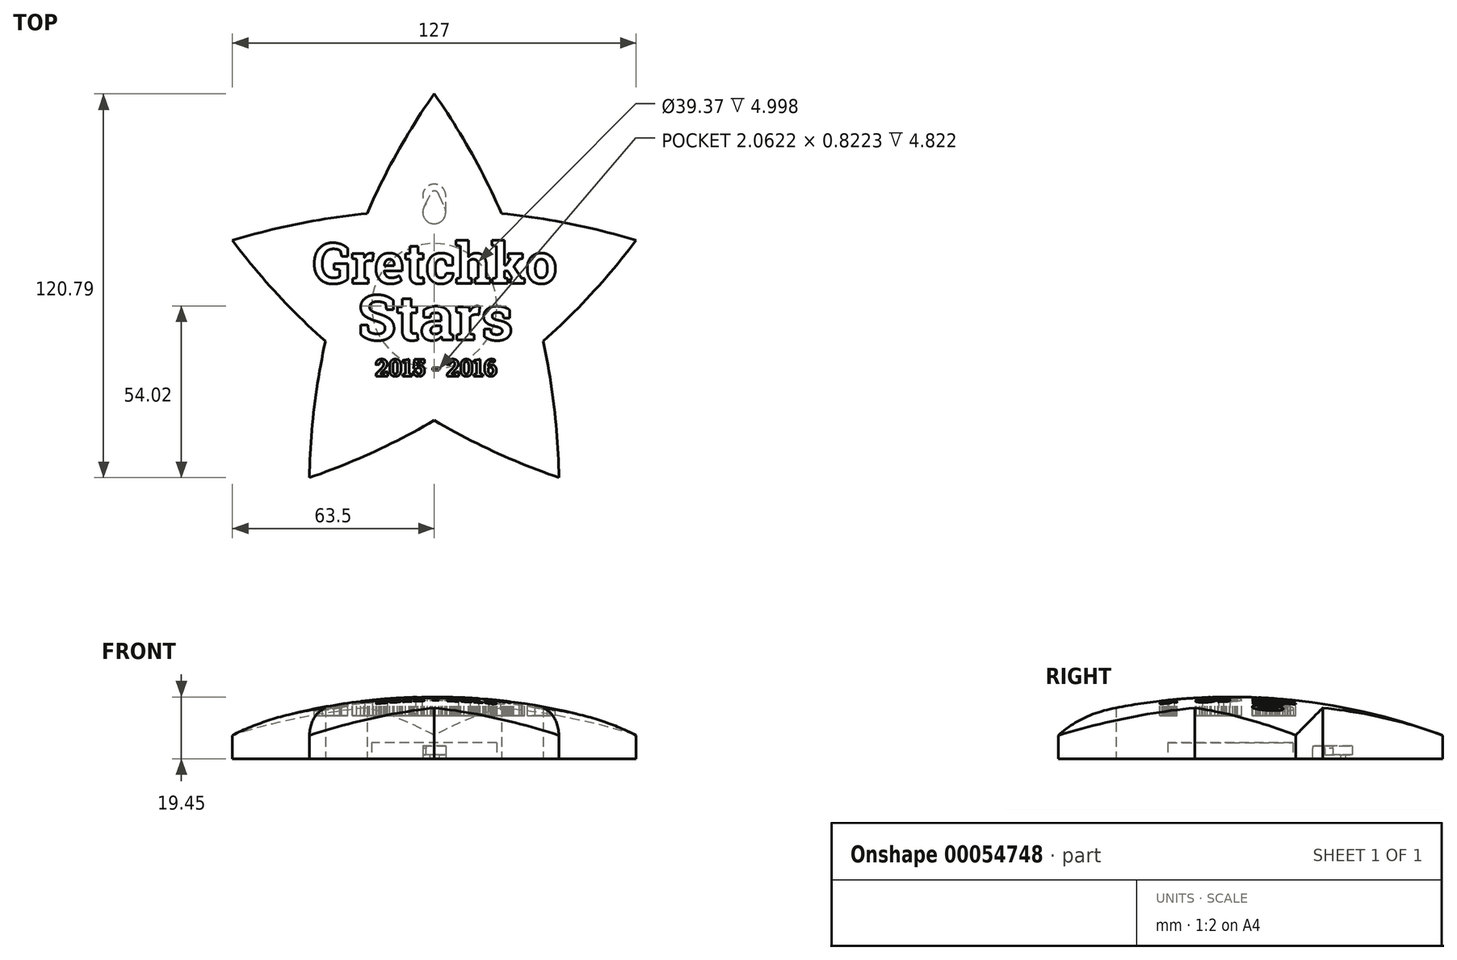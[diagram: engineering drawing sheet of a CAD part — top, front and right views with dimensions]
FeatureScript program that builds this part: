
annotation { "Feature Type Name" : "Feature", "Feature Type Description" : "" }
export const myFeature = defineFeature(function(context is Context, id is Id, definition is map)
    precondition{}
    {
        {
            var Q0;
            Q0=qCreatedBy(makeId("Top.planeOp"),FACE);
            var sketch = newSketch(context, id + "F0", { "sketchPlane" : qUnion([Q0])});
            skArc(sketch, "E0", {"start": v(39.25, -54.02) * mm, "mid": v(28.67, 9.31) * mm, "end": v(0, 66.77) * mm});
            skArc(sketch, "E1", {"start": v(0, 66.77) * mm, "mid": v(-28.67, 9.31) * mm, "end": v(-39.25, -54.02) * mm});
            skArc(sketch, "E2", {"start": v(63.5, 20.63) * mm, "mid": v(0, 30.14) * mm, "end": v(-63.5, 20.63) * mm});
            skArc(sketch, "E3", {"start": v(-63.5, 20.63) * mm, "mid": v(-17.72, -24.39) * mm, "end": v(39.25, -54.02) * mm});
            skArc(sketch, "E4", {"start": v(-39.25, -54.02) * mm, "mid": v(17.72, -24.39) * mm, "end": v(63.5, 20.63) * mm});
            skSolve(sketch);
        }
        {
            var Q0;
            Q0 = qSketchRegion(id + "F0", true);
            extrude(context, id + "F1", {"entities" : qUnion([Q0]), "depth" : 67.5 * mm});
        }
        {
            var Q0;
            Q0=qCreatedBy(makeId("Top.planeOp"),FACE);
            var sketch = newSketch(context, id + "F2", { "sketchPlane" : qUnion([Q0])});
            skCircle(sketch, "E5", {"center": v(0, 0) * mm, "radius": 190.5 * mm});
            skLineSegment(sketch, "E6", {"start": v(0, 190.5) * mm, "end": v(0, -190.5) * mm});
            skSolve(sketch);
        }
        {
            var Q0;
            Q0=makeQuery(id+"F1.opExtrude","SWEPT_BODY",BODY,{"disambiguationData":[OSD([sQuery(id+"F0.wireOp",EDGE,"E0"),sQuery(id+"F0.wireOp",EDGE,"E1"),sQuery(id+"F0.wireOp",EDGE,"E2"),sQuery(id+"F0.wireOp",EDGE,"E3"),sQuery(id+"F0.wireOp",EDGE,"E4")])]});
            var Q1;
            Q1=makeQuery(id+"F1.opExtrude","SWEPT_EDGE",EDGE,{"disambiguationData":[OSD([sQuery(id+"F0.wireOp",EDGE,"E2"),sQuery(id+"F0.wireOp",EDGE,"E3")])]});
            var Q2;
            Q2=makeQuery(id+"F1.opExtrude","CAP_FACE",FACE,{"disambiguationData":[OSD([sQuery(id+"F0.wireOp",EDGE,"E0"),sQuery(id+"F0.wireOp",EDGE,"E1"),sQuery(id+"F0.wireOp",EDGE,"E2"),sQuery(id+"F0.wireOp",EDGE,"E3"),sQuery(id+"F0.wireOp",EDGE,"E4")])],"isStart":false});
            transform(context, id + "F3", {"entities" : qUnion([Q0]), "transformType" : TransformType.TRANSLATION_DISTANCE, "transformDirection" : qUnion([Q2]), "distance" : 171.05 * mm, "makeCopy" : false});
        }
        {
            var Q0;
            {var subQ0=sQuery(id+"F2.wireOp",EDGE,"E6");Q0=makeQuery(id+"F2.imprint","IMPRINT",FACE,{"disambiguationData":[TD([[makeQuery(id+"F2.imprint","IMPRINT",EDGE,{"derivedFrom":subQ0}),-1.0]])]});}
            var Q1;
            Q1=sQuery(id+"F2.wireOp",EDGE,"E6");
            revolve(context, id + "F4", {"entities" : qUnion([Q0]), "axis" : qUnion([Q1]), "revolveType" : RevolveType.FULL});
        }
        {
            var Q0;
            Q0=makeQuery(id+"F1.opExtrude","SWEPT_BODY",BODY,{"disambiguationData":[OSD([sQuery(id+"F0.wireOp",EDGE,"E0"),sQuery(id+"F0.wireOp",EDGE,"E1"),sQuery(id+"F0.wireOp",EDGE,"E2"),sQuery(id+"F0.wireOp",EDGE,"E3"),sQuery(id+"F0.wireOp",EDGE,"E4")])]});
            var Q1;
            Q1=makeQuery(id+"F4.opRevolve","SWEPT_BODY",BODY,{"disambiguationData":[OSD([sQuery(id+"F2.wireOp",EDGE,"E5"),sQuery(id+"F2.wireOp",EDGE,"E6")])]});
            booleanBodies(context, id + "F5", {"operationType" : BooleanOperationType.INTERSECTION, "tools" : qUnion([Q0, Q1])});
        }
        {
            var Q0;
            Q0=qCreatedBy(makeId("Top.planeOp"),FACE);
            var sketch = newSketch(context, id + "F6", { "sketchPlane" : qUnion([Q0])});
            skText(sketch, "E7", { "text": "Gretchko", "fontName": "RobotoSlab-Bold.ttf"});
            skLineSegment(sketch, "E8", {"start": v(0, 0) * mm, "end": v(0, 66.71) * mm});
            const initialGuessF6  = {"E7": [-0.03813, 0.0071, 1, 0, 0.0128]};
            skSetInitialGuess(sketch, initialGuessF6);
            skSolve(sketch);
        }
        {
            var Q0;
            Q0=qCreatedBy(makeId("Top.planeOp"),FACE);
            var sketch = newSketch(context, id + "F7", { "sketchPlane" : qUnion([Q0])});
            skText(sketch, "E9", { "text": "Stars", "fontName": "RobotoSlab-Bold.ttf"});
            const initialGuessF7  = {"E9": [-0.02408, -0.01073, 1, 0, 0.01428]};
            skSetInitialGuess(sketch, initialGuessF7);
            skSolve(sketch);
        }
        {
            var Q0;
            Q0=qCreatedBy(makeId("Top.planeOp"),FACE);
            var sketch = newSketch(context, id + "F8", { "sketchPlane" : qUnion([Q0])});
            skText(sketch, "E10", { "text": "2015 - 2016", "fontName": "RobotoSlab-Bold.ttf"});
            const initialGuessF8  = {"E10": [-0.01854, -0.0221, 1, 0, 0.00539]};
            skSetInitialGuess(sketch, initialGuessF8);
            skSolve(sketch);
        }
        {
            var Q0;
            Q0=makeQuery(id+"F5.opBoolean","INTERSECT",BODY,{"derivedFrom":[makeQuery(id+"F1.opExtrude","SWEPT_BODY",BODY,{"disambiguationData":[OSD([sQuery(id+"F0.wireOp",EDGE,"E0"),sQuery(id+"F0.wireOp",EDGE,"E1"),sQuery(id+"F0.wireOp",EDGE,"E2"),sQuery(id+"F0.wireOp",EDGE,"E3"),sQuery(id+"F0.wireOp",EDGE,"E4")])]}),makeQuery(id+"F4.opRevolve","SWEPT_BODY",BODY,{"disambiguationData":[OSD([sQuery(id+"F2.wireOp",EDGE,"E5"),sQuery(id+"F2.wireOp",EDGE,"E6")])]})]});
            var Q1;
            Q1=qCreatedBy(makeId("Top.planeOp"),FACE);
            transform(context, id + "F9", {"entities" : qUnion([Q0]), "transformType" : TransformType.TRANSLATION_DISTANCE, "transformDirection" : qUnion([Q1]), "distance" : 221.94 * mm, "oppositeDirection" : true, "makeCopy" : false});
        }
        {
            var Q0;
            Q0=makeQuery(id+"F6.imprint","IMPRINT",FACE,{"disambiguationData":[TD([[makeQuery(id+"F6.imprint","IMPRINT",EDGE,{"derivedFrom":sQuery(id+"F6.wireOp",EDGE,"E7.sketch_text.stroke-0")}),-1.0]])]});
            var Q1;
            Q1=makeQuery(id+"F6.imprint","IMPRINT",FACE,{"disambiguationData":[TD([[makeQuery(id+"F6.imprint","IMPRINT",EDGE,{"derivedFrom":sQuery(id+"F6.wireOp",EDGE,"E7.sketch_text.stroke-26")}),-1.0]])]});
            var Q2;
            Q2=makeQuery(id+"F6.imprint","IMPRINT",FACE,{"disambiguationData":[TD([[makeQuery(id+"F6.imprint","IMPRINT",EDGE,{"derivedFrom":sQuery(id+"F6.wireOp",EDGE,"E7.sketch_text.stroke-69")}),-1.0]])]});
            var Q3;
            Q3=makeQuery(id+"F6.imprint","IMPRINT",FACE,{"disambiguationData":[TD([[makeQuery(id+"F6.imprint","IMPRINT",EDGE,{"derivedFrom":sQuery(id+"F6.wireOp",EDGE,"E7.sketch_text.stroke-112")}),-1.0]])]});
            var Q4;
            Q4=makeQuery(id+"F6.imprint","IMPRINT",FACE,{"disambiguationData":[TD([[makeQuery(id+"F6.imprint","IMPRINT",EDGE,{"derivedFrom":sQuery(id+"F6.wireOp",EDGE,"E7.sketch_text.stroke-138")}),-1.0]])]});
            var Q5;
            Q5=makeQuery(id+"F6.imprint","IMPRINT",FACE,{"disambiguationData":[TD([[makeQuery(id+"F6.imprint","IMPRINT",EDGE,{"derivedFrom":sQuery(id+"F6.wireOp",EDGE,"E7.sketch_text.stroke-45")}),-1.0]])]});
            var Q6;
            Q6=makeQuery(id+"F6.imprint","IMPRINT",FACE,{"disambiguationData":[TD([[makeQuery(id+"F6.imprint","IMPRINT",EDGE,{"derivedFrom":sQuery(id+"F6.wireOp",EDGE,"E7.sketch_text.stroke-89")}),-1.0]])]});
            var Q7;
            {var subQ1=sQuery(id+"F6.wireOp",EDGE,"E7.sketch_text.stroke-96");Q7=makeQuery(id+"F6.imprint","IMPRINT",FACE,{"disambiguationData":[TD([[makeQuery(id+"F6.imprint","IMPRINT",EDGE,{"derivedFrom":subQ1}),-1.0]])]});}
            var Q8;
            Q8=makeQuery(id+"F6.imprint","IMPRINT",FACE,{"disambiguationData":[TD([[makeQuery(id+"F6.imprint","IMPRINT",EDGE,{"derivedFrom":sQuery(id+"F6.wireOp",EDGE,"E7.sketch_text.stroke-165")}),-1.0]])]});
            var Q9;
            Q9=makeQuery(id+"F7.imprint","IMPRINT",FACE,{"disambiguationData":[TD([[makeQuery(id+"F7.imprint","IMPRINT",EDGE,{"derivedFrom":sQuery(id+"F7.wireOp",EDGE,"E9.sketch_text.stroke-0")}),-1.0]])]});
            var Q10;
            Q10=makeQuery(id+"F7.imprint","IMPRINT",FACE,{"disambiguationData":[TD([[makeQuery(id+"F7.imprint","IMPRINT",EDGE,{"derivedFrom":sQuery(id+"F7.wireOp",EDGE,"E9.sketch_text.stroke-30")}),-1.0]])]});
            var Q11;
            Q11=makeQuery(id+"F7.imprint","IMPRINT",FACE,{"disambiguationData":[TD([[makeQuery(id+"F7.imprint","IMPRINT",EDGE,{"derivedFrom":sQuery(id+"F7.wireOp",EDGE,"E9.sketch_text.stroke-85")}),-1.0]])]});
            var Q12;
            Q12=makeQuery(id+"F7.imprint","IMPRINT",FACE,{"disambiguationData":[TD([[makeQuery(id+"F7.imprint","IMPRINT",EDGE,{"derivedFrom":sQuery(id+"F7.wireOp",EDGE,"E9.sketch_text.stroke-104")}),-1.0]])]});
            var Q13;
            Q13=makeQuery(id+"F7.imprint","IMPRINT",FACE,{"disambiguationData":[TD([[makeQuery(id+"F7.imprint","IMPRINT",EDGE,{"derivedFrom":sQuery(id+"F7.wireOp",EDGE,"E9.sketch_text.stroke-50")}),-1.0]])]});
            var Q14;
            Q14=makeQuery(id+"F8.imprint","IMPRINT",FACE,{"disambiguationData":[TD([[makeQuery(id+"F8.imprint","IMPRINT",EDGE,{"derivedFrom":sQuery(id+"F8.wireOp",EDGE,"E10.sketch_text.stroke-0")}),-1.0]])]});
            var Q15;
            Q15=makeQuery(id+"F8.imprint","IMPRINT",FACE,{"disambiguationData":[TD([[makeQuery(id+"F8.imprint","IMPRINT",EDGE,{"derivedFrom":sQuery(id+"F8.wireOp",EDGE,"E10.sketch_text.stroke-43")}),-1.0]])]});
            var Q16;
            Q16=makeQuery(id+"F8.imprint","IMPRINT",FACE,{"disambiguationData":[TD([[makeQuery(id+"F8.imprint","IMPRINT",EDGE,{"derivedFrom":sQuery(id+"F8.wireOp",EDGE,"E10.sketch_text.stroke-53")}),-1.0]])]});
            var Q17;
            Q17=makeQuery(id+"F8.imprint","IMPRINT",FACE,{"disambiguationData":[TD([[makeQuery(id+"F8.imprint","IMPRINT",EDGE,{"derivedFrom":sQuery(id+"F8.wireOp",EDGE,"E10.sketch_text.stroke-79")}),-1.0]])]});
            var Q18;
            Q18=makeQuery(id+"F8.imprint","IMPRINT",FACE,{"disambiguationData":[TD([[makeQuery(id+"F8.imprint","IMPRINT",EDGE,{"derivedFrom":sQuery(id+"F8.wireOp",EDGE,"E10.sketch_text.stroke-83")}),-1.0]])]});
            var Q19;
            Q19=makeQuery(id+"F8.imprint","IMPRINT",FACE,{"disambiguationData":[TD([[makeQuery(id+"F8.imprint","IMPRINT",EDGE,{"derivedFrom":sQuery(id+"F8.wireOp",EDGE,"E10.sketch_text.stroke-126")}),-1.0]])]});
            var Q20;
            Q20=makeQuery(id+"F8.imprint","IMPRINT",FACE,{"disambiguationData":[TD([[makeQuery(id+"F8.imprint","IMPRINT",EDGE,{"derivedFrom":sQuery(id+"F8.wireOp",EDGE,"E10.sketch_text.stroke-23")}),-1.0]])]});
            var Q21;
            Q21=makeQuery(id+"F8.imprint","IMPRINT",FACE,{"disambiguationData":[TD([[makeQuery(id+"F8.imprint","IMPRINT",EDGE,{"derivedFrom":sQuery(id+"F8.wireOp",EDGE,"E10.sketch_text.stroke-106")}),-1.0]])]});
            var Q22;
            Q22=makeQuery(id+"F8.imprint","IMPRINT",FACE,{"disambiguationData":[TD([[makeQuery(id+"F8.imprint","IMPRINT",EDGE,{"derivedFrom":sQuery(id+"F8.wireOp",EDGE,"E10.sketch_text.stroke-136")}),-1.0]])]});
            extrude(context, id + "F10", {"entities" : qUnion([Q0, Q1, Q2, Q3, Q4, Q5, Q6, Q7, Q8, Q9, Q10, Q11, Q12, Q13, Q14, Q15, Q16, Q17, Q18, Q19, Q20, Q21, Q22]), "operationType" : NewBodyOperationType.ADD, "oppositeDirection" : true, "depth" : 15.68 * mm});
        }
        {
            var Q0;
            Q0=makeQuery(id+"F10.opExtrude","SWEPT_BODY",BODY,{"disambiguationData":[OSD([sQuery(id+"F6.wireOp",EDGE,"E7.sketch_text.stroke-0"),sQuery(id+"F6.wireOp",EDGE,"E7.sketch_text.stroke-1"),sQuery(id+"F6.wireOp",EDGE,"E7.sketch_text.stroke-2"),sQuery(id+"F6.wireOp",EDGE,"E7.sketch_text.stroke-3"),sQuery(id+"F6.wireOp",EDGE,"E7.sketch_text.stroke-4"),sQuery(id+"F6.wireOp",EDGE,"E7.sketch_text.stroke-5"),sQuery(id+"F6.wireOp",EDGE,"E7.sketch_text.stroke-6"),sQuery(id+"F6.wireOp",EDGE,"E7.sketch_text.stroke-7"),sQuery(id+"F6.wireOp",EDGE,"E7.sketch_text.stroke-8"),sQuery(id+"F6.wireOp",EDGE,"E7.sketch_text.stroke-9"),sQuery(id+"F6.wireOp",EDGE,"E7.sketch_text.stroke-10"),sQuery(id+"F6.wireOp",EDGE,"E7.sketch_text.stroke-11"),sQuery(id+"F6.wireOp",EDGE,"E7.sketch_text.stroke-12"),sQuery(id+"F6.wireOp",EDGE,"E7.sketch_text.stroke-13"),sQuery(id+"F6.wireOp",EDGE,"E7.sketch_text.stroke-14"),sQuery(id+"F6.wireOp",EDGE,"E7.sketch_text.stroke-15"),sQuery(id+"F6.wireOp",EDGE,"E7.sketch_text.stroke-16"),sQuery(id+"F6.wireOp",EDGE,"E7.sketch_text.stroke-17"),sQuery(id+"F6.wireOp",EDGE,"E7.sketch_text.stroke-18"),sQuery(id+"F6.wireOp",EDGE,"E7.sketch_text.stroke-19"),sQuery(id+"F6.wireOp",EDGE,"E7.sketch_text.stroke-20"),sQuery(id+"F6.wireOp",EDGE,"E7.sketch_text.stroke-21"),sQuery(id+"F6.wireOp",EDGE,"E7.sketch_text.stroke-22"),sQuery(id+"F6.wireOp",EDGE,"E7.sketch_text.stroke-23"),sQuery(id+"F6.wireOp",EDGE,"E7.sketch_text.stroke-24"),sQuery(id+"F6.wireOp",EDGE,"E7.sketch_text.stroke-25")])]});
            var Q1;
            Q1=makeQuery(id+"F10.opExtrude","SWEPT_BODY",BODY,{"disambiguationData":[OSD([sQuery(id+"F6.wireOp",EDGE,"E7.sketch_text.stroke-26"),sQuery(id+"F6.wireOp",EDGE,"E7.sketch_text.stroke-27"),sQuery(id+"F6.wireOp",EDGE,"E7.sketch_text.stroke-28"),sQuery(id+"F6.wireOp",EDGE,"E7.sketch_text.stroke-29"),sQuery(id+"F6.wireOp",EDGE,"E7.sketch_text.stroke-30"),sQuery(id+"F6.wireOp",EDGE,"E7.sketch_text.stroke-31"),sQuery(id+"F6.wireOp",EDGE,"E7.sketch_text.stroke-32"),sQuery(id+"F6.wireOp",EDGE,"E7.sketch_text.stroke-33"),sQuery(id+"F6.wireOp",EDGE,"E7.sketch_text.stroke-34"),sQuery(id+"F6.wireOp",EDGE,"E7.sketch_text.stroke-35"),sQuery(id+"F6.wireOp",EDGE,"E7.sketch_text.stroke-36"),sQuery(id+"F6.wireOp",EDGE,"E7.sketch_text.stroke-37"),sQuery(id+"F6.wireOp",EDGE,"E7.sketch_text.stroke-38"),sQuery(id+"F6.wireOp",EDGE,"E7.sketch_text.stroke-39"),sQuery(id+"F6.wireOp",EDGE,"E7.sketch_text.stroke-40"),sQuery(id+"F6.wireOp",EDGE,"E7.sketch_text.stroke-41"),sQuery(id+"F6.wireOp",EDGE,"E7.sketch_text.stroke-42"),sQuery(id+"F6.wireOp",EDGE,"E7.sketch_text.stroke-43"),sQuery(id+"F6.wireOp",EDGE,"E7.sketch_text.stroke-44")])]});
            var Q2;
            Q2=makeQuery(id+"F10.opExtrude","SWEPT_BODY",BODY,{"disambiguationData":[OSD([sQuery(id+"F6.wireOp",EDGE,"E7.sketch_text.stroke-45"),sQuery(id+"F6.wireOp",EDGE,"E7.sketch_text.stroke-46"),sQuery(id+"F6.wireOp",EDGE,"E7.sketch_text.stroke-47"),sQuery(id+"F6.wireOp",EDGE,"E7.sketch_text.stroke-48"),sQuery(id+"F6.wireOp",EDGE,"E7.sketch_text.stroke-49"),sQuery(id+"F6.wireOp",EDGE,"E7.sketch_text.stroke-50"),sQuery(id+"F6.wireOp",EDGE,"E7.sketch_text.stroke-51"),sQuery(id+"F6.wireOp",EDGE,"E7.sketch_text.stroke-52"),sQuery(id+"F6.wireOp",EDGE,"E7.sketch_text.stroke-53"),sQuery(id+"F6.wireOp",EDGE,"E7.sketch_text.stroke-54"),sQuery(id+"F6.wireOp",EDGE,"E7.sketch_text.stroke-55"),sQuery(id+"F6.wireOp",EDGE,"E7.sketch_text.stroke-56"),sQuery(id+"F6.wireOp",EDGE,"E7.sketch_text.stroke-57"),sQuery(id+"F6.wireOp",EDGE,"E7.sketch_text.stroke-58"),sQuery(id+"F6.wireOp",EDGE,"E7.sketch_text.stroke-59"),sQuery(id+"F6.wireOp",EDGE,"E7.sketch_text.stroke-60"),sQuery(id+"F6.wireOp",EDGE,"E7.sketch_text.stroke-61"),sQuery(id+"F6.wireOp",EDGE,"E7.sketch_text.stroke-62"),sQuery(id+"F6.wireOp",EDGE,"E7.sketch_text.stroke-63"),sQuery(id+"F6.wireOp",EDGE,"E7.sketch_text.stroke-64"),sQuery(id+"F6.wireOp",EDGE,"E7.sketch_text.stroke-65"),sQuery(id+"F6.wireOp",EDGE,"E7.sketch_text.stroke-66"),sQuery(id+"F6.wireOp",EDGE,"E7.sketch_text.stroke-67"),sQuery(id+"F6.wireOp",EDGE,"E7.sketch_text.stroke-68")])]});
            var Q3;
            Q3=makeQuery(id+"F10.opExtrude","SWEPT_BODY",BODY,{"disambiguationData":[OSD([sQuery(id+"F6.wireOp",EDGE,"E7.sketch_text.stroke-69"),sQuery(id+"F6.wireOp",EDGE,"E7.sketch_text.stroke-70"),sQuery(id+"F6.wireOp",EDGE,"E7.sketch_text.stroke-71"),sQuery(id+"F6.wireOp",EDGE,"E7.sketch_text.stroke-72"),sQuery(id+"F6.wireOp",EDGE,"E7.sketch_text.stroke-73"),sQuery(id+"F6.wireOp",EDGE,"E7.sketch_text.stroke-74"),sQuery(id+"F6.wireOp",EDGE,"E7.sketch_text.stroke-75"),sQuery(id+"F6.wireOp",EDGE,"E7.sketch_text.stroke-76"),sQuery(id+"F6.wireOp",EDGE,"E7.sketch_text.stroke-77"),sQuery(id+"F6.wireOp",EDGE,"E7.sketch_text.stroke-78"),sQuery(id+"F6.wireOp",EDGE,"E7.sketch_text.stroke-79"),sQuery(id+"F6.wireOp",EDGE,"E7.sketch_text.stroke-80"),sQuery(id+"F6.wireOp",EDGE,"E7.sketch_text.stroke-81"),sQuery(id+"F6.wireOp",EDGE,"E7.sketch_text.stroke-82"),sQuery(id+"F6.wireOp",EDGE,"E7.sketch_text.stroke-83"),sQuery(id+"F6.wireOp",EDGE,"E7.sketch_text.stroke-84"),sQuery(id+"F6.wireOp",EDGE,"E7.sketch_text.stroke-85"),sQuery(id+"F6.wireOp",EDGE,"E7.sketch_text.stroke-86"),sQuery(id+"F6.wireOp",EDGE,"E7.sketch_text.stroke-87"),sQuery(id+"F6.wireOp",EDGE,"E7.sketch_text.stroke-88")])]});
            var Q4;
            Q4=makeQuery(id+"F10.opExtrude","SWEPT_BODY",BODY,{"disambiguationData":[OSD([sQuery(id+"F6.wireOp",EDGE,"E7.sketch_text.stroke-89"),sQuery(id+"F6.wireOp",EDGE,"E7.sketch_text.stroke-90"),sQuery(id+"F6.wireOp",EDGE,"E7.sketch_text.stroke-91"),sQuery(id+"F6.wireOp",EDGE,"E7.sketch_text.stroke-92"),sQuery(id+"F6.wireOp",EDGE,"E7.sketch_text.stroke-93"),sQuery(id+"F6.wireOp",EDGE,"E7.sketch_text.stroke-94"),sQuery(id+"F6.wireOp",EDGE,"E7.sketch_text.stroke-95"),sQuery(id+"F6.wireOp",EDGE,"E7.sketch_text.stroke-96"),sQuery(id+"F6.wireOp",EDGE,"E7.sketch_text.stroke-97"),sQuery(id+"F6.wireOp",EDGE,"E7.sketch_text.stroke-98"),sQuery(id+"F6.wireOp",EDGE,"E7.sketch_text.stroke-99"),sQuery(id+"F6.wireOp",EDGE,"E7.sketch_text.stroke-100"),sQuery(id+"F6.wireOp",EDGE,"E7.sketch_text.stroke-101"),sQuery(id+"F6.wireOp",EDGE,"E7.sketch_text.stroke-102"),sQuery(id+"F6.wireOp",EDGE,"E7.sketch_text.stroke-103"),sQuery(id+"F6.wireOp",EDGE,"E7.sketch_text.stroke-104"),sQuery(id+"F6.wireOp",EDGE,"E7.sketch_text.stroke-105"),sQuery(id+"F6.wireOp",EDGE,"E7.sketch_text.stroke-106"),sQuery(id+"F6.wireOp",EDGE,"E7.sketch_text.stroke-107"),sQuery(id+"F6.wireOp",EDGE,"E7.sketch_text.stroke-108"),sQuery(id+"F6.wireOp",EDGE,"E7.sketch_text.stroke-109"),sQuery(id+"F6.wireOp",EDGE,"E7.sketch_text.stroke-110"),sQuery(id+"F6.wireOp",EDGE,"E7.sketch_text.stroke-111")])]});
            var Q5;
            Q5=makeQuery(id+"F10.opExtrude","SWEPT_BODY",BODY,{"disambiguationData":[OSD([sQuery(id+"F6.wireOp",EDGE,"E7.sketch_text.stroke-112"),sQuery(id+"F6.wireOp",EDGE,"E7.sketch_text.stroke-113"),sQuery(id+"F6.wireOp",EDGE,"E7.sketch_text.stroke-114"),sQuery(id+"F6.wireOp",EDGE,"E7.sketch_text.stroke-115"),sQuery(id+"F6.wireOp",EDGE,"E7.sketch_text.stroke-116"),sQuery(id+"F6.wireOp",EDGE,"E7.sketch_text.stroke-117"),sQuery(id+"F6.wireOp",EDGE,"E7.sketch_text.stroke-118"),sQuery(id+"F6.wireOp",EDGE,"E7.sketch_text.stroke-119"),sQuery(id+"F6.wireOp",EDGE,"E7.sketch_text.stroke-120"),sQuery(id+"F6.wireOp",EDGE,"E7.sketch_text.stroke-121"),sQuery(id+"F6.wireOp",EDGE,"E7.sketch_text.stroke-122"),sQuery(id+"F6.wireOp",EDGE,"E7.sketch_text.stroke-123"),sQuery(id+"F6.wireOp",EDGE,"E7.sketch_text.stroke-124"),sQuery(id+"F6.wireOp",EDGE,"E7.sketch_text.stroke-125"),sQuery(id+"F6.wireOp",EDGE,"E7.sketch_text.stroke-126"),sQuery(id+"F6.wireOp",EDGE,"E7.sketch_text.stroke-127"),sQuery(id+"F6.wireOp",EDGE,"E7.sketch_text.stroke-128"),sQuery(id+"F6.wireOp",EDGE,"E7.sketch_text.stroke-129"),sQuery(id+"F6.wireOp",EDGE,"E7.sketch_text.stroke-130"),sQuery(id+"F6.wireOp",EDGE,"E7.sketch_text.stroke-131"),sQuery(id+"F6.wireOp",EDGE,"E7.sketch_text.stroke-132"),sQuery(id+"F6.wireOp",EDGE,"E7.sketch_text.stroke-133"),sQuery(id+"F6.wireOp",EDGE,"E7.sketch_text.stroke-134"),sQuery(id+"F6.wireOp",EDGE,"E7.sketch_text.stroke-135"),sQuery(id+"F6.wireOp",EDGE,"E7.sketch_text.stroke-136"),sQuery(id+"F6.wireOp",EDGE,"E7.sketch_text.stroke-137")])]});
            var Q6;
            Q6=makeQuery(id+"F10.opExtrude","SWEPT_BODY",BODY,{"disambiguationData":[OSD([sQuery(id+"F6.wireOp",EDGE,"E7.sketch_text.stroke-138"),sQuery(id+"F6.wireOp",EDGE,"E7.sketch_text.stroke-139"),sQuery(id+"F6.wireOp",EDGE,"E7.sketch_text.stroke-140"),sQuery(id+"F6.wireOp",EDGE,"E7.sketch_text.stroke-141"),sQuery(id+"F6.wireOp",EDGE,"E7.sketch_text.stroke-142"),sQuery(id+"F6.wireOp",EDGE,"E7.sketch_text.stroke-143"),sQuery(id+"F6.wireOp",EDGE,"E7.sketch_text.stroke-144"),sQuery(id+"F6.wireOp",EDGE,"E7.sketch_text.stroke-145"),sQuery(id+"F6.wireOp",EDGE,"E7.sketch_text.stroke-146"),sQuery(id+"F6.wireOp",EDGE,"E7.sketch_text.stroke-147"),sQuery(id+"F6.wireOp",EDGE,"E7.sketch_text.stroke-148"),sQuery(id+"F6.wireOp",EDGE,"E7.sketch_text.stroke-149"),sQuery(id+"F6.wireOp",EDGE,"E7.sketch_text.stroke-150"),sQuery(id+"F6.wireOp",EDGE,"E7.sketch_text.stroke-151"),sQuery(id+"F6.wireOp",EDGE,"E7.sketch_text.stroke-152"),sQuery(id+"F6.wireOp",EDGE,"E7.sketch_text.stroke-153"),sQuery(id+"F6.wireOp",EDGE,"E7.sketch_text.stroke-154"),sQuery(id+"F6.wireOp",EDGE,"E7.sketch_text.stroke-155"),sQuery(id+"F6.wireOp",EDGE,"E7.sketch_text.stroke-156"),sQuery(id+"F6.wireOp",EDGE,"E7.sketch_text.stroke-157"),sQuery(id+"F6.wireOp",EDGE,"E7.sketch_text.stroke-158"),sQuery(id+"F6.wireOp",EDGE,"E7.sketch_text.stroke-159"),sQuery(id+"F6.wireOp",EDGE,"E7.sketch_text.stroke-160"),sQuery(id+"F6.wireOp",EDGE,"E7.sketch_text.stroke-161"),sQuery(id+"F6.wireOp",EDGE,"E7.sketch_text.stroke-162"),sQuery(id+"F6.wireOp",EDGE,"E7.sketch_text.stroke-163"),sQuery(id+"F6.wireOp",EDGE,"E7.sketch_text.stroke-164")])]});
            var Q7;
            Q7=makeQuery(id+"F10.opExtrude","SWEPT_BODY",BODY,{"disambiguationData":[OSD([sQuery(id+"F6.wireOp",EDGE,"E7.sketch_text.stroke-165"),sQuery(id+"F6.wireOp",EDGE,"E7.sketch_text.stroke-166"),sQuery(id+"F6.wireOp",EDGE,"E7.sketch_text.stroke-167"),sQuery(id+"F6.wireOp",EDGE,"E7.sketch_text.stroke-168"),sQuery(id+"F6.wireOp",EDGE,"E7.sketch_text.stroke-169"),sQuery(id+"F6.wireOp",EDGE,"E7.sketch_text.stroke-170"),sQuery(id+"F6.wireOp",EDGE,"E7.sketch_text.stroke-171"),sQuery(id+"F6.wireOp",EDGE,"E7.sketch_text.stroke-172"),sQuery(id+"F6.wireOp",EDGE,"E7.sketch_text.stroke-173"),sQuery(id+"F6.wireOp",EDGE,"E7.sketch_text.stroke-174"),sQuery(id+"F6.wireOp",EDGE,"E7.sketch_text.stroke-175"),sQuery(id+"F6.wireOp",EDGE,"E7.sketch_text.stroke-176"),sQuery(id+"F6.wireOp",EDGE,"E7.sketch_text.stroke-177"),sQuery(id+"F6.wireOp",EDGE,"E7.sketch_text.stroke-178"),sQuery(id+"F6.wireOp",EDGE,"E7.sketch_text.stroke-179"),sQuery(id+"F6.wireOp",EDGE,"E7.sketch_text.stroke-180"),sQuery(id+"F6.wireOp",EDGE,"E7.sketch_text.stroke-181"),sQuery(id+"F6.wireOp",EDGE,"E7.sketch_text.stroke-182"),sQuery(id+"F6.wireOp",EDGE,"E7.sketch_text.stroke-183"),sQuery(id+"F6.wireOp",EDGE,"E7.sketch_text.stroke-184")])]});
            var Q8;
            Q8=makeQuery(id+"F10.opExtrude","SWEPT_BODY",BODY,{"disambiguationData":[OSD([sQuery(id+"F7.wireOp",EDGE,"E9.sketch_text.stroke-0"),sQuery(id+"F7.wireOp",EDGE,"E9.sketch_text.stroke-1"),sQuery(id+"F7.wireOp",EDGE,"E9.sketch_text.stroke-2"),sQuery(id+"F7.wireOp",EDGE,"E9.sketch_text.stroke-3"),sQuery(id+"F7.wireOp",EDGE,"E9.sketch_text.stroke-4"),sQuery(id+"F7.wireOp",EDGE,"E9.sketch_text.stroke-5"),sQuery(id+"F7.wireOp",EDGE,"E9.sketch_text.stroke-6"),sQuery(id+"F7.wireOp",EDGE,"E9.sketch_text.stroke-7"),sQuery(id+"F7.wireOp",EDGE,"E9.sketch_text.stroke-8"),sQuery(id+"F7.wireOp",EDGE,"E9.sketch_text.stroke-9"),sQuery(id+"F7.wireOp",EDGE,"E9.sketch_text.stroke-10"),sQuery(id+"F7.wireOp",EDGE,"E9.sketch_text.stroke-11"),sQuery(id+"F7.wireOp",EDGE,"E9.sketch_text.stroke-12"),sQuery(id+"F7.wireOp",EDGE,"E9.sketch_text.stroke-13"),sQuery(id+"F7.wireOp",EDGE,"E9.sketch_text.stroke-14"),sQuery(id+"F7.wireOp",EDGE,"E9.sketch_text.stroke-15"),sQuery(id+"F7.wireOp",EDGE,"E9.sketch_text.stroke-16"),sQuery(id+"F7.wireOp",EDGE,"E9.sketch_text.stroke-17"),sQuery(id+"F7.wireOp",EDGE,"E9.sketch_text.stroke-18"),sQuery(id+"F7.wireOp",EDGE,"E9.sketch_text.stroke-19"),sQuery(id+"F7.wireOp",EDGE,"E9.sketch_text.stroke-20"),sQuery(id+"F7.wireOp",EDGE,"E9.sketch_text.stroke-21"),sQuery(id+"F7.wireOp",EDGE,"E9.sketch_text.stroke-22"),sQuery(id+"F7.wireOp",EDGE,"E9.sketch_text.stroke-23"),sQuery(id+"F7.wireOp",EDGE,"E9.sketch_text.stroke-24"),sQuery(id+"F7.wireOp",EDGE,"E9.sketch_text.stroke-25"),sQuery(id+"F7.wireOp",EDGE,"E9.sketch_text.stroke-26"),sQuery(id+"F7.wireOp",EDGE,"E9.sketch_text.stroke-27"),sQuery(id+"F7.wireOp",EDGE,"E9.sketch_text.stroke-28"),sQuery(id+"F7.wireOp",EDGE,"E9.sketch_text.stroke-29")])]});
            var Q9;
            Q9=makeQuery(id+"F10.opExtrude","SWEPT_BODY",BODY,{"disambiguationData":[OSD([sQuery(id+"F7.wireOp",EDGE,"E9.sketch_text.stroke-30"),sQuery(id+"F7.wireOp",EDGE,"E9.sketch_text.stroke-31"),sQuery(id+"F7.wireOp",EDGE,"E9.sketch_text.stroke-32"),sQuery(id+"F7.wireOp",EDGE,"E9.sketch_text.stroke-33"),sQuery(id+"F7.wireOp",EDGE,"E9.sketch_text.stroke-34"),sQuery(id+"F7.wireOp",EDGE,"E9.sketch_text.stroke-35"),sQuery(id+"F7.wireOp",EDGE,"E9.sketch_text.stroke-36"),sQuery(id+"F7.wireOp",EDGE,"E9.sketch_text.stroke-37"),sQuery(id+"F7.wireOp",EDGE,"E9.sketch_text.stroke-38"),sQuery(id+"F7.wireOp",EDGE,"E9.sketch_text.stroke-39"),sQuery(id+"F7.wireOp",EDGE,"E9.sketch_text.stroke-40"),sQuery(id+"F7.wireOp",EDGE,"E9.sketch_text.stroke-41"),sQuery(id+"F7.wireOp",EDGE,"E9.sketch_text.stroke-42"),sQuery(id+"F7.wireOp",EDGE,"E9.sketch_text.stroke-43"),sQuery(id+"F7.wireOp",EDGE,"E9.sketch_text.stroke-44"),sQuery(id+"F7.wireOp",EDGE,"E9.sketch_text.stroke-45"),sQuery(id+"F7.wireOp",EDGE,"E9.sketch_text.stroke-46"),sQuery(id+"F7.wireOp",EDGE,"E9.sketch_text.stroke-47"),sQuery(id+"F7.wireOp",EDGE,"E9.sketch_text.stroke-48"),sQuery(id+"F7.wireOp",EDGE,"E9.sketch_text.stroke-49")])]});
            var Q10;
            Q10=makeQuery(id+"F10.opExtrude","SWEPT_BODY",BODY,{"disambiguationData":[OSD([sQuery(id+"F7.wireOp",EDGE,"E9.sketch_text.stroke-50"),sQuery(id+"F7.wireOp",EDGE,"E9.sketch_text.stroke-51"),sQuery(id+"F7.wireOp",EDGE,"E9.sketch_text.stroke-52"),sQuery(id+"F7.wireOp",EDGE,"E9.sketch_text.stroke-53"),sQuery(id+"F7.wireOp",EDGE,"E9.sketch_text.stroke-54"),sQuery(id+"F7.wireOp",EDGE,"E9.sketch_text.stroke-55"),sQuery(id+"F7.wireOp",EDGE,"E9.sketch_text.stroke-56"),sQuery(id+"F7.wireOp",EDGE,"E9.sketch_text.stroke-57"),sQuery(id+"F7.wireOp",EDGE,"E9.sketch_text.stroke-58"),sQuery(id+"F7.wireOp",EDGE,"E9.sketch_text.stroke-59"),sQuery(id+"F7.wireOp",EDGE,"E9.sketch_text.stroke-60"),sQuery(id+"F7.wireOp",EDGE,"E9.sketch_text.stroke-61"),sQuery(id+"F7.wireOp",EDGE,"E9.sketch_text.stroke-62"),sQuery(id+"F7.wireOp",EDGE,"E9.sketch_text.stroke-63"),sQuery(id+"F7.wireOp",EDGE,"E9.sketch_text.stroke-64"),sQuery(id+"F7.wireOp",EDGE,"E9.sketch_text.stroke-65"),sQuery(id+"F7.wireOp",EDGE,"E9.sketch_text.stroke-66"),sQuery(id+"F7.wireOp",EDGE,"E9.sketch_text.stroke-67"),sQuery(id+"F7.wireOp",EDGE,"E9.sketch_text.stroke-68"),sQuery(id+"F7.wireOp",EDGE,"E9.sketch_text.stroke-69"),sQuery(id+"F7.wireOp",EDGE,"E9.sketch_text.stroke-70"),sQuery(id+"F7.wireOp",EDGE,"E9.sketch_text.stroke-71"),sQuery(id+"F7.wireOp",EDGE,"E9.sketch_text.stroke-72"),sQuery(id+"F7.wireOp",EDGE,"E9.sketch_text.stroke-73"),sQuery(id+"F7.wireOp",EDGE,"E9.sketch_text.stroke-74"),sQuery(id+"F7.wireOp",EDGE,"E9.sketch_text.stroke-75"),sQuery(id+"F7.wireOp",EDGE,"E9.sketch_text.stroke-76"),sQuery(id+"F7.wireOp",EDGE,"E9.sketch_text.stroke-77"),sQuery(id+"F7.wireOp",EDGE,"E9.sketch_text.stroke-78"),sQuery(id+"F7.wireOp",EDGE,"E9.sketch_text.stroke-79"),sQuery(id+"F7.wireOp",EDGE,"E9.sketch_text.stroke-80"),sQuery(id+"F7.wireOp",EDGE,"E9.sketch_text.stroke-81"),sQuery(id+"F7.wireOp",EDGE,"E9.sketch_text.stroke-82"),sQuery(id+"F7.wireOp",EDGE,"E9.sketch_text.stroke-83"),sQuery(id+"F7.wireOp",EDGE,"E9.sketch_text.stroke-84")])]});
            var Q11;
            Q11=makeQuery(id+"F10.opExtrude","SWEPT_BODY",BODY,{"disambiguationData":[OSD([sQuery(id+"F7.wireOp",EDGE,"E9.sketch_text.stroke-85"),sQuery(id+"F7.wireOp",EDGE,"E9.sketch_text.stroke-86"),sQuery(id+"F7.wireOp",EDGE,"E9.sketch_text.stroke-87"),sQuery(id+"F7.wireOp",EDGE,"E9.sketch_text.stroke-88"),sQuery(id+"F7.wireOp",EDGE,"E9.sketch_text.stroke-89"),sQuery(id+"F7.wireOp",EDGE,"E9.sketch_text.stroke-90"),sQuery(id+"F7.wireOp",EDGE,"E9.sketch_text.stroke-91"),sQuery(id+"F7.wireOp",EDGE,"E9.sketch_text.stroke-92"),sQuery(id+"F7.wireOp",EDGE,"E9.sketch_text.stroke-93"),sQuery(id+"F7.wireOp",EDGE,"E9.sketch_text.stroke-94"),sQuery(id+"F7.wireOp",EDGE,"E9.sketch_text.stroke-95"),sQuery(id+"F7.wireOp",EDGE,"E9.sketch_text.stroke-96"),sQuery(id+"F7.wireOp",EDGE,"E9.sketch_text.stroke-97"),sQuery(id+"F7.wireOp",EDGE,"E9.sketch_text.stroke-98"),sQuery(id+"F7.wireOp",EDGE,"E9.sketch_text.stroke-99"),sQuery(id+"F7.wireOp",EDGE,"E9.sketch_text.stroke-100"),sQuery(id+"F7.wireOp",EDGE,"E9.sketch_text.stroke-101"),sQuery(id+"F7.wireOp",EDGE,"E9.sketch_text.stroke-102"),sQuery(id+"F7.wireOp",EDGE,"E9.sketch_text.stroke-103")])]});
            var Q12;
            Q12=makeQuery(id+"F10.opExtrude","SWEPT_BODY",BODY,{"disambiguationData":[OSD([sQuery(id+"F7.wireOp",EDGE,"E9.sketch_text.stroke-104"),sQuery(id+"F7.wireOp",EDGE,"E9.sketch_text.stroke-105"),sQuery(id+"F7.wireOp",EDGE,"E9.sketch_text.stroke-106"),sQuery(id+"F7.wireOp",EDGE,"E9.sketch_text.stroke-107"),sQuery(id+"F7.wireOp",EDGE,"E9.sketch_text.stroke-108"),sQuery(id+"F7.wireOp",EDGE,"E9.sketch_text.stroke-109"),sQuery(id+"F7.wireOp",EDGE,"E9.sketch_text.stroke-110"),sQuery(id+"F7.wireOp",EDGE,"E9.sketch_text.stroke-111"),sQuery(id+"F7.wireOp",EDGE,"E9.sketch_text.stroke-112"),sQuery(id+"F7.wireOp",EDGE,"E9.sketch_text.stroke-113"),sQuery(id+"F7.wireOp",EDGE,"E9.sketch_text.stroke-114"),sQuery(id+"F7.wireOp",EDGE,"E9.sketch_text.stroke-115"),sQuery(id+"F7.wireOp",EDGE,"E9.sketch_text.stroke-116"),sQuery(id+"F7.wireOp",EDGE,"E9.sketch_text.stroke-117"),sQuery(id+"F7.wireOp",EDGE,"E9.sketch_text.stroke-118"),sQuery(id+"F7.wireOp",EDGE,"E9.sketch_text.stroke-119"),sQuery(id+"F7.wireOp",EDGE,"E9.sketch_text.stroke-120"),sQuery(id+"F7.wireOp",EDGE,"E9.sketch_text.stroke-121"),sQuery(id+"F7.wireOp",EDGE,"E9.sketch_text.stroke-122"),sQuery(id+"F7.wireOp",EDGE,"E9.sketch_text.stroke-123"),sQuery(id+"F7.wireOp",EDGE,"E9.sketch_text.stroke-124"),sQuery(id+"F7.wireOp",EDGE,"E9.sketch_text.stroke-125"),sQuery(id+"F7.wireOp",EDGE,"E9.sketch_text.stroke-126"),sQuery(id+"F7.wireOp",EDGE,"E9.sketch_text.stroke-127"),sQuery(id+"F7.wireOp",EDGE,"E9.sketch_text.stroke-128"),sQuery(id+"F7.wireOp",EDGE,"E9.sketch_text.stroke-129"),sQuery(id+"F7.wireOp",EDGE,"E9.sketch_text.stroke-130"),sQuery(id+"F7.wireOp",EDGE,"E9.sketch_text.stroke-131"),sQuery(id+"F7.wireOp",EDGE,"E9.sketch_text.stroke-132"),sQuery(id+"F7.wireOp",EDGE,"E9.sketch_text.stroke-133")])]});
            var Q13;
            Q13=makeQuery(id+"F10.opExtrude","SWEPT_BODY",BODY,{"disambiguationData":[OSD([sQuery(id+"F8.wireOp",EDGE,"E10.sketch_text.stroke-0"),sQuery(id+"F8.wireOp",EDGE,"E10.sketch_text.stroke-1"),sQuery(id+"F8.wireOp",EDGE,"E10.sketch_text.stroke-2"),sQuery(id+"F8.wireOp",EDGE,"E10.sketch_text.stroke-3"),sQuery(id+"F8.wireOp",EDGE,"E10.sketch_text.stroke-4"),sQuery(id+"F8.wireOp",EDGE,"E10.sketch_text.stroke-5"),sQuery(id+"F8.wireOp",EDGE,"E10.sketch_text.stroke-6"),sQuery(id+"F8.wireOp",EDGE,"E10.sketch_text.stroke-7"),sQuery(id+"F8.wireOp",EDGE,"E10.sketch_text.stroke-8"),sQuery(id+"F8.wireOp",EDGE,"E10.sketch_text.stroke-9"),sQuery(id+"F8.wireOp",EDGE,"E10.sketch_text.stroke-10"),sQuery(id+"F8.wireOp",EDGE,"E10.sketch_text.stroke-11"),sQuery(id+"F8.wireOp",EDGE,"E10.sketch_text.stroke-12"),sQuery(id+"F8.wireOp",EDGE,"E10.sketch_text.stroke-13"),sQuery(id+"F8.wireOp",EDGE,"E10.sketch_text.stroke-14"),sQuery(id+"F8.wireOp",EDGE,"E10.sketch_text.stroke-15"),sQuery(id+"F8.wireOp",EDGE,"E10.sketch_text.stroke-16"),sQuery(id+"F8.wireOp",EDGE,"E10.sketch_text.stroke-17"),sQuery(id+"F8.wireOp",EDGE,"E10.sketch_text.stroke-18"),sQuery(id+"F8.wireOp",EDGE,"E10.sketch_text.stroke-19"),sQuery(id+"F8.wireOp",EDGE,"E10.sketch_text.stroke-20"),sQuery(id+"F8.wireOp",EDGE,"E10.sketch_text.stroke-21"),sQuery(id+"F8.wireOp",EDGE,"E10.sketch_text.stroke-22")])]});
            var Q14;
            Q14=makeQuery(id+"F10.opExtrude","SWEPT_BODY",BODY,{"disambiguationData":[OSD([sQuery(id+"F8.wireOp",EDGE,"E10.sketch_text.stroke-23"),sQuery(id+"F8.wireOp",EDGE,"E10.sketch_text.stroke-24"),sQuery(id+"F8.wireOp",EDGE,"E10.sketch_text.stroke-25"),sQuery(id+"F8.wireOp",EDGE,"E10.sketch_text.stroke-26"),sQuery(id+"F8.wireOp",EDGE,"E10.sketch_text.stroke-27"),sQuery(id+"F8.wireOp",EDGE,"E10.sketch_text.stroke-28"),sQuery(id+"F8.wireOp",EDGE,"E10.sketch_text.stroke-29"),sQuery(id+"F8.wireOp",EDGE,"E10.sketch_text.stroke-30"),sQuery(id+"F8.wireOp",EDGE,"E10.sketch_text.stroke-31"),sQuery(id+"F8.wireOp",EDGE,"E10.sketch_text.stroke-32"),sQuery(id+"F8.wireOp",EDGE,"E10.sketch_text.stroke-33"),sQuery(id+"F8.wireOp",EDGE,"E10.sketch_text.stroke-34"),sQuery(id+"F8.wireOp",EDGE,"E10.sketch_text.stroke-35"),sQuery(id+"F8.wireOp",EDGE,"E10.sketch_text.stroke-36"),sQuery(id+"F8.wireOp",EDGE,"E10.sketch_text.stroke-37"),sQuery(id+"F8.wireOp",EDGE,"E10.sketch_text.stroke-38"),sQuery(id+"F8.wireOp",EDGE,"E10.sketch_text.stroke-39"),sQuery(id+"F8.wireOp",EDGE,"E10.sketch_text.stroke-40"),sQuery(id+"F8.wireOp",EDGE,"E10.sketch_text.stroke-41"),sQuery(id+"F8.wireOp",EDGE,"E10.sketch_text.stroke-42")])]});
            var Q15;
            Q15=makeQuery(id+"F10.opExtrude","SWEPT_BODY",BODY,{"disambiguationData":[OSD([sQuery(id+"F8.wireOp",EDGE,"E10.sketch_text.stroke-43"),sQuery(id+"F8.wireOp",EDGE,"E10.sketch_text.stroke-44"),sQuery(id+"F8.wireOp",EDGE,"E10.sketch_text.stroke-45"),sQuery(id+"F8.wireOp",EDGE,"E10.sketch_text.stroke-46"),sQuery(id+"F8.wireOp",EDGE,"E10.sketch_text.stroke-47"),sQuery(id+"F8.wireOp",EDGE,"E10.sketch_text.stroke-48"),sQuery(id+"F8.wireOp",EDGE,"E10.sketch_text.stroke-49"),sQuery(id+"F8.wireOp",EDGE,"E10.sketch_text.stroke-50"),sQuery(id+"F8.wireOp",EDGE,"E10.sketch_text.stroke-51"),sQuery(id+"F8.wireOp",EDGE,"E10.sketch_text.stroke-52")])]});
            var Q16;
            Q16=makeQuery(id+"F10.opExtrude","SWEPT_BODY",BODY,{"disambiguationData":[OSD([sQuery(id+"F8.wireOp",EDGE,"E10.sketch_text.stroke-53"),sQuery(id+"F8.wireOp",EDGE,"E10.sketch_text.stroke-54"),sQuery(id+"F8.wireOp",EDGE,"E10.sketch_text.stroke-55"),sQuery(id+"F8.wireOp",EDGE,"E10.sketch_text.stroke-56"),sQuery(id+"F8.wireOp",EDGE,"E10.sketch_text.stroke-57"),sQuery(id+"F8.wireOp",EDGE,"E10.sketch_text.stroke-58"),sQuery(id+"F8.wireOp",EDGE,"E10.sketch_text.stroke-59"),sQuery(id+"F8.wireOp",EDGE,"E10.sketch_text.stroke-60"),sQuery(id+"F8.wireOp",EDGE,"E10.sketch_text.stroke-61"),sQuery(id+"F8.wireOp",EDGE,"E10.sketch_text.stroke-62"),sQuery(id+"F8.wireOp",EDGE,"E10.sketch_text.stroke-63"),sQuery(id+"F8.wireOp",EDGE,"E10.sketch_text.stroke-64"),sQuery(id+"F8.wireOp",EDGE,"E10.sketch_text.stroke-65"),sQuery(id+"F8.wireOp",EDGE,"E10.sketch_text.stroke-66"),sQuery(id+"F8.wireOp",EDGE,"E10.sketch_text.stroke-67"),sQuery(id+"F8.wireOp",EDGE,"E10.sketch_text.stroke-68"),sQuery(id+"F8.wireOp",EDGE,"E10.sketch_text.stroke-69"),sQuery(id+"F8.wireOp",EDGE,"E10.sketch_text.stroke-70"),sQuery(id+"F8.wireOp",EDGE,"E10.sketch_text.stroke-71"),sQuery(id+"F8.wireOp",EDGE,"E10.sketch_text.stroke-72"),sQuery(id+"F8.wireOp",EDGE,"E10.sketch_text.stroke-73"),sQuery(id+"F8.wireOp",EDGE,"E10.sketch_text.stroke-74"),sQuery(id+"F8.wireOp",EDGE,"E10.sketch_text.stroke-75"),sQuery(id+"F8.wireOp",EDGE,"E10.sketch_text.stroke-76"),sQuery(id+"F8.wireOp",EDGE,"E10.sketch_text.stroke-77"),sQuery(id+"F8.wireOp",EDGE,"E10.sketch_text.stroke-78")])]});
            var Q17;
            Q17=makeQuery(id+"F10.opExtrude","SWEPT_BODY",BODY,{"disambiguationData":[OSD([sQuery(id+"F8.wireOp",EDGE,"E10.sketch_text.stroke-79"),sQuery(id+"F8.wireOp",EDGE,"E10.sketch_text.stroke-80"),sQuery(id+"F8.wireOp",EDGE,"E10.sketch_text.stroke-81"),sQuery(id+"F8.wireOp",EDGE,"E10.sketch_text.stroke-82")])]});
            var Q18;
            Q18=makeQuery(id+"F10.opExtrude","SWEPT_BODY",BODY,{"disambiguationData":[OSD([sQuery(id+"F8.wireOp",EDGE,"E10.sketch_text.stroke-83"),sQuery(id+"F8.wireOp",EDGE,"E10.sketch_text.stroke-84"),sQuery(id+"F8.wireOp",EDGE,"E10.sketch_text.stroke-85"),sQuery(id+"F8.wireOp",EDGE,"E10.sketch_text.stroke-86"),sQuery(id+"F8.wireOp",EDGE,"E10.sketch_text.stroke-87"),sQuery(id+"F8.wireOp",EDGE,"E10.sketch_text.stroke-88"),sQuery(id+"F8.wireOp",EDGE,"E10.sketch_text.stroke-89"),sQuery(id+"F8.wireOp",EDGE,"E10.sketch_text.stroke-90"),sQuery(id+"F8.wireOp",EDGE,"E10.sketch_text.stroke-91"),sQuery(id+"F8.wireOp",EDGE,"E10.sketch_text.stroke-92"),sQuery(id+"F8.wireOp",EDGE,"E10.sketch_text.stroke-93"),sQuery(id+"F8.wireOp",EDGE,"E10.sketch_text.stroke-94"),sQuery(id+"F8.wireOp",EDGE,"E10.sketch_text.stroke-95"),sQuery(id+"F8.wireOp",EDGE,"E10.sketch_text.stroke-96"),sQuery(id+"F8.wireOp",EDGE,"E10.sketch_text.stroke-97"),sQuery(id+"F8.wireOp",EDGE,"E10.sketch_text.stroke-98"),sQuery(id+"F8.wireOp",EDGE,"E10.sketch_text.stroke-99"),sQuery(id+"F8.wireOp",EDGE,"E10.sketch_text.stroke-100"),sQuery(id+"F8.wireOp",EDGE,"E10.sketch_text.stroke-101"),sQuery(id+"F8.wireOp",EDGE,"E10.sketch_text.stroke-102"),sQuery(id+"F8.wireOp",EDGE,"E10.sketch_text.stroke-103"),sQuery(id+"F8.wireOp",EDGE,"E10.sketch_text.stroke-104"),sQuery(id+"F8.wireOp",EDGE,"E10.sketch_text.stroke-105")])]});
            var Q19;
            Q19=makeQuery(id+"F10.opExtrude","SWEPT_BODY",BODY,{"disambiguationData":[OSD([sQuery(id+"F8.wireOp",EDGE,"E10.sketch_text.stroke-106"),sQuery(id+"F8.wireOp",EDGE,"E10.sketch_text.stroke-107"),sQuery(id+"F8.wireOp",EDGE,"E10.sketch_text.stroke-108"),sQuery(id+"F8.wireOp",EDGE,"E10.sketch_text.stroke-109"),sQuery(id+"F8.wireOp",EDGE,"E10.sketch_text.stroke-110"),sQuery(id+"F8.wireOp",EDGE,"E10.sketch_text.stroke-111"),sQuery(id+"F8.wireOp",EDGE,"E10.sketch_text.stroke-112"),sQuery(id+"F8.wireOp",EDGE,"E10.sketch_text.stroke-113"),sQuery(id+"F8.wireOp",EDGE,"E10.sketch_text.stroke-114"),sQuery(id+"F8.wireOp",EDGE,"E10.sketch_text.stroke-115"),sQuery(id+"F8.wireOp",EDGE,"E10.sketch_text.stroke-116"),sQuery(id+"F8.wireOp",EDGE,"E10.sketch_text.stroke-117"),sQuery(id+"F8.wireOp",EDGE,"E10.sketch_text.stroke-118"),sQuery(id+"F8.wireOp",EDGE,"E10.sketch_text.stroke-119"),sQuery(id+"F8.wireOp",EDGE,"E10.sketch_text.stroke-120"),sQuery(id+"F8.wireOp",EDGE,"E10.sketch_text.stroke-121"),sQuery(id+"F8.wireOp",EDGE,"E10.sketch_text.stroke-122"),sQuery(id+"F8.wireOp",EDGE,"E10.sketch_text.stroke-123"),sQuery(id+"F8.wireOp",EDGE,"E10.sketch_text.stroke-124"),sQuery(id+"F8.wireOp",EDGE,"E10.sketch_text.stroke-125")])]});
            var Q20;
            Q20=makeQuery(id+"F10.opExtrude","SWEPT_BODY",BODY,{"disambiguationData":[OSD([sQuery(id+"F8.wireOp",EDGE,"E10.sketch_text.stroke-126"),sQuery(id+"F8.wireOp",EDGE,"E10.sketch_text.stroke-127"),sQuery(id+"F8.wireOp",EDGE,"E10.sketch_text.stroke-128"),sQuery(id+"F8.wireOp",EDGE,"E10.sketch_text.stroke-129"),sQuery(id+"F8.wireOp",EDGE,"E10.sketch_text.stroke-130"),sQuery(id+"F8.wireOp",EDGE,"E10.sketch_text.stroke-131"),sQuery(id+"F8.wireOp",EDGE,"E10.sketch_text.stroke-132"),sQuery(id+"F8.wireOp",EDGE,"E10.sketch_text.stroke-133"),sQuery(id+"F8.wireOp",EDGE,"E10.sketch_text.stroke-134"),sQuery(id+"F8.wireOp",EDGE,"E10.sketch_text.stroke-135")])]});
            var Q21;
            Q21=makeQuery(id+"F10.opExtrude","SWEPT_BODY",BODY,{"disambiguationData":[OSD([sQuery(id+"F8.wireOp",EDGE,"E10.sketch_text.stroke-136"),sQuery(id+"F8.wireOp",EDGE,"E10.sketch_text.stroke-137"),sQuery(id+"F8.wireOp",EDGE,"E10.sketch_text.stroke-138"),sQuery(id+"F8.wireOp",EDGE,"E10.sketch_text.stroke-139"),sQuery(id+"F8.wireOp",EDGE,"E10.sketch_text.stroke-140"),sQuery(id+"F8.wireOp",EDGE,"E10.sketch_text.stroke-141"),sQuery(id+"F8.wireOp",EDGE,"E10.sketch_text.stroke-142"),sQuery(id+"F8.wireOp",EDGE,"E10.sketch_text.stroke-143"),sQuery(id+"F8.wireOp",EDGE,"E10.sketch_text.stroke-144"),sQuery(id+"F8.wireOp",EDGE,"E10.sketch_text.stroke-145"),sQuery(id+"F8.wireOp",EDGE,"E10.sketch_text.stroke-146"),sQuery(id+"F8.wireOp",EDGE,"E10.sketch_text.stroke-147"),sQuery(id+"F8.wireOp",EDGE,"E10.sketch_text.stroke-148"),sQuery(id+"F8.wireOp",EDGE,"E10.sketch_text.stroke-149"),sQuery(id+"F8.wireOp",EDGE,"E10.sketch_text.stroke-150"),sQuery(id+"F8.wireOp",EDGE,"E10.sketch_text.stroke-151"),sQuery(id+"F8.wireOp",EDGE,"E10.sketch_text.stroke-152"),sQuery(id+"F8.wireOp",EDGE,"E10.sketch_text.stroke-153"),sQuery(id+"F8.wireOp",EDGE,"E10.sketch_text.stroke-154"),sQuery(id+"F8.wireOp",EDGE,"E10.sketch_text.stroke-155"),sQuery(id+"F8.wireOp",EDGE,"E10.sketch_text.stroke-156"),sQuery(id+"F8.wireOp",EDGE,"E10.sketch_text.stroke-157"),sQuery(id+"F8.wireOp",EDGE,"E10.sketch_text.stroke-158"),sQuery(id+"F8.wireOp",EDGE,"E10.sketch_text.stroke-159"),sQuery(id+"F8.wireOp",EDGE,"E10.sketch_text.stroke-160"),sQuery(id+"F8.wireOp",EDGE,"E10.sketch_text.stroke-161"),sQuery(id+"F8.wireOp",EDGE,"E10.sketch_text.stroke-162"),sQuery(id+"F8.wireOp",EDGE,"E10.sketch_text.stroke-163")])]});
            var Q22;
            Q22=qCreatedBy(makeId("Top.planeOp"),FACE);
            transform(context, id + "F11", {"entities" : qUnion([Q0, Q1, Q2, Q3, Q4, Q5, Q6, Q7, Q8, Q9, Q10, Q11, Q12, Q13, Q14, Q15, Q16, Q17, Q18, Q19, Q20, Q21]), "transformType" : TransformType.TRANSLATION_DISTANCE, "transformDirection" : qUnion([Q22]), "distance" : 21.66 * mm, "oppositeDirection" : true, "makeCopy" : false});
        }
        {
            var Q0;
            Q0=makeQuery(id+"F10.opExtrude","SWEPT_BODY",BODY,{"disambiguationData":[OSD([sQuery(id+"F6.wireOp",EDGE,"E7.sketch_text.stroke-0"),sQuery(id+"F6.wireOp",EDGE,"E7.sketch_text.stroke-1"),sQuery(id+"F6.wireOp",EDGE,"E7.sketch_text.stroke-2"),sQuery(id+"F6.wireOp",EDGE,"E7.sketch_text.stroke-3"),sQuery(id+"F6.wireOp",EDGE,"E7.sketch_text.stroke-4"),sQuery(id+"F6.wireOp",EDGE,"E7.sketch_text.stroke-5"),sQuery(id+"F6.wireOp",EDGE,"E7.sketch_text.stroke-6"),sQuery(id+"F6.wireOp",EDGE,"E7.sketch_text.stroke-7"),sQuery(id+"F6.wireOp",EDGE,"E7.sketch_text.stroke-8"),sQuery(id+"F6.wireOp",EDGE,"E7.sketch_text.stroke-9"),sQuery(id+"F6.wireOp",EDGE,"E7.sketch_text.stroke-10"),sQuery(id+"F6.wireOp",EDGE,"E7.sketch_text.stroke-11"),sQuery(id+"F6.wireOp",EDGE,"E7.sketch_text.stroke-12"),sQuery(id+"F6.wireOp",EDGE,"E7.sketch_text.stroke-13"),sQuery(id+"F6.wireOp",EDGE,"E7.sketch_text.stroke-14"),sQuery(id+"F6.wireOp",EDGE,"E7.sketch_text.stroke-15"),sQuery(id+"F6.wireOp",EDGE,"E7.sketch_text.stroke-16"),sQuery(id+"F6.wireOp",EDGE,"E7.sketch_text.stroke-17"),sQuery(id+"F6.wireOp",EDGE,"E7.sketch_text.stroke-18"),sQuery(id+"F6.wireOp",EDGE,"E7.sketch_text.stroke-19"),sQuery(id+"F6.wireOp",EDGE,"E7.sketch_text.stroke-20"),sQuery(id+"F6.wireOp",EDGE,"E7.sketch_text.stroke-21"),sQuery(id+"F6.wireOp",EDGE,"E7.sketch_text.stroke-22"),sQuery(id+"F6.wireOp",EDGE,"E7.sketch_text.stroke-23"),sQuery(id+"F6.wireOp",EDGE,"E7.sketch_text.stroke-24"),sQuery(id+"F6.wireOp",EDGE,"E7.sketch_text.stroke-25")])]});
            var Q1;
            Q1=makeQuery(id+"F10.opExtrude","SWEPT_BODY",BODY,{"disambiguationData":[OSD([sQuery(id+"F6.wireOp",EDGE,"E7.sketch_text.stroke-26"),sQuery(id+"F6.wireOp",EDGE,"E7.sketch_text.stroke-27"),sQuery(id+"F6.wireOp",EDGE,"E7.sketch_text.stroke-28"),sQuery(id+"F6.wireOp",EDGE,"E7.sketch_text.stroke-29"),sQuery(id+"F6.wireOp",EDGE,"E7.sketch_text.stroke-30"),sQuery(id+"F6.wireOp",EDGE,"E7.sketch_text.stroke-31"),sQuery(id+"F6.wireOp",EDGE,"E7.sketch_text.stroke-32"),sQuery(id+"F6.wireOp",EDGE,"E7.sketch_text.stroke-33"),sQuery(id+"F6.wireOp",EDGE,"E7.sketch_text.stroke-34"),sQuery(id+"F6.wireOp",EDGE,"E7.sketch_text.stroke-35"),sQuery(id+"F6.wireOp",EDGE,"E7.sketch_text.stroke-36"),sQuery(id+"F6.wireOp",EDGE,"E7.sketch_text.stroke-37"),sQuery(id+"F6.wireOp",EDGE,"E7.sketch_text.stroke-38"),sQuery(id+"F6.wireOp",EDGE,"E7.sketch_text.stroke-39"),sQuery(id+"F6.wireOp",EDGE,"E7.sketch_text.stroke-40"),sQuery(id+"F6.wireOp",EDGE,"E7.sketch_text.stroke-41"),sQuery(id+"F6.wireOp",EDGE,"E7.sketch_text.stroke-42"),sQuery(id+"F6.wireOp",EDGE,"E7.sketch_text.stroke-43"),sQuery(id+"F6.wireOp",EDGE,"E7.sketch_text.stroke-44")])]});
            var Q2;
            Q2=makeQuery(id+"F10.opExtrude","SWEPT_BODY",BODY,{"disambiguationData":[OSD([sQuery(id+"F6.wireOp",EDGE,"E7.sketch_text.stroke-45"),sQuery(id+"F6.wireOp",EDGE,"E7.sketch_text.stroke-46"),sQuery(id+"F6.wireOp",EDGE,"E7.sketch_text.stroke-47"),sQuery(id+"F6.wireOp",EDGE,"E7.sketch_text.stroke-48"),sQuery(id+"F6.wireOp",EDGE,"E7.sketch_text.stroke-49"),sQuery(id+"F6.wireOp",EDGE,"E7.sketch_text.stroke-50"),sQuery(id+"F6.wireOp",EDGE,"E7.sketch_text.stroke-51"),sQuery(id+"F6.wireOp",EDGE,"E7.sketch_text.stroke-52"),sQuery(id+"F6.wireOp",EDGE,"E7.sketch_text.stroke-53"),sQuery(id+"F6.wireOp",EDGE,"E7.sketch_text.stroke-54"),sQuery(id+"F6.wireOp",EDGE,"E7.sketch_text.stroke-55"),sQuery(id+"F6.wireOp",EDGE,"E7.sketch_text.stroke-56"),sQuery(id+"F6.wireOp",EDGE,"E7.sketch_text.stroke-57"),sQuery(id+"F6.wireOp",EDGE,"E7.sketch_text.stroke-58"),sQuery(id+"F6.wireOp",EDGE,"E7.sketch_text.stroke-59"),sQuery(id+"F6.wireOp",EDGE,"E7.sketch_text.stroke-60"),sQuery(id+"F6.wireOp",EDGE,"E7.sketch_text.stroke-61"),sQuery(id+"F6.wireOp",EDGE,"E7.sketch_text.stroke-62"),sQuery(id+"F6.wireOp",EDGE,"E7.sketch_text.stroke-63"),sQuery(id+"F6.wireOp",EDGE,"E7.sketch_text.stroke-64"),sQuery(id+"F6.wireOp",EDGE,"E7.sketch_text.stroke-65"),sQuery(id+"F6.wireOp",EDGE,"E7.sketch_text.stroke-66"),sQuery(id+"F6.wireOp",EDGE,"E7.sketch_text.stroke-67"),sQuery(id+"F6.wireOp",EDGE,"E7.sketch_text.stroke-68")])]});
            var Q3;
            Q3=makeQuery(id+"F10.opExtrude","SWEPT_BODY",BODY,{"disambiguationData":[OSD([sQuery(id+"F6.wireOp",EDGE,"E7.sketch_text.stroke-69"),sQuery(id+"F6.wireOp",EDGE,"E7.sketch_text.stroke-70"),sQuery(id+"F6.wireOp",EDGE,"E7.sketch_text.stroke-71"),sQuery(id+"F6.wireOp",EDGE,"E7.sketch_text.stroke-72"),sQuery(id+"F6.wireOp",EDGE,"E7.sketch_text.stroke-73"),sQuery(id+"F6.wireOp",EDGE,"E7.sketch_text.stroke-74"),sQuery(id+"F6.wireOp",EDGE,"E7.sketch_text.stroke-75"),sQuery(id+"F6.wireOp",EDGE,"E7.sketch_text.stroke-76"),sQuery(id+"F6.wireOp",EDGE,"E7.sketch_text.stroke-77"),sQuery(id+"F6.wireOp",EDGE,"E7.sketch_text.stroke-78"),sQuery(id+"F6.wireOp",EDGE,"E7.sketch_text.stroke-79"),sQuery(id+"F6.wireOp",EDGE,"E7.sketch_text.stroke-80"),sQuery(id+"F6.wireOp",EDGE,"E7.sketch_text.stroke-81"),sQuery(id+"F6.wireOp",EDGE,"E7.sketch_text.stroke-82"),sQuery(id+"F6.wireOp",EDGE,"E7.sketch_text.stroke-83"),sQuery(id+"F6.wireOp",EDGE,"E7.sketch_text.stroke-84"),sQuery(id+"F6.wireOp",EDGE,"E7.sketch_text.stroke-85"),sQuery(id+"F6.wireOp",EDGE,"E7.sketch_text.stroke-86"),sQuery(id+"F6.wireOp",EDGE,"E7.sketch_text.stroke-87"),sQuery(id+"F6.wireOp",EDGE,"E7.sketch_text.stroke-88")])]});
            var Q4;
            Q4=makeQuery(id+"F10.opExtrude","SWEPT_BODY",BODY,{"disambiguationData":[OSD([sQuery(id+"F6.wireOp",EDGE,"E7.sketch_text.stroke-89"),sQuery(id+"F6.wireOp",EDGE,"E7.sketch_text.stroke-90"),sQuery(id+"F6.wireOp",EDGE,"E7.sketch_text.stroke-91"),sQuery(id+"F6.wireOp",EDGE,"E7.sketch_text.stroke-92"),sQuery(id+"F6.wireOp",EDGE,"E7.sketch_text.stroke-93"),sQuery(id+"F6.wireOp",EDGE,"E7.sketch_text.stroke-94"),sQuery(id+"F6.wireOp",EDGE,"E7.sketch_text.stroke-95"),sQuery(id+"F6.wireOp",EDGE,"E7.sketch_text.stroke-96"),sQuery(id+"F6.wireOp",EDGE,"E7.sketch_text.stroke-97"),sQuery(id+"F6.wireOp",EDGE,"E7.sketch_text.stroke-98"),sQuery(id+"F6.wireOp",EDGE,"E7.sketch_text.stroke-99"),sQuery(id+"F6.wireOp",EDGE,"E7.sketch_text.stroke-100"),sQuery(id+"F6.wireOp",EDGE,"E7.sketch_text.stroke-101"),sQuery(id+"F6.wireOp",EDGE,"E7.sketch_text.stroke-102"),sQuery(id+"F6.wireOp",EDGE,"E7.sketch_text.stroke-103"),sQuery(id+"F6.wireOp",EDGE,"E7.sketch_text.stroke-104"),sQuery(id+"F6.wireOp",EDGE,"E7.sketch_text.stroke-105"),sQuery(id+"F6.wireOp",EDGE,"E7.sketch_text.stroke-106"),sQuery(id+"F6.wireOp",EDGE,"E7.sketch_text.stroke-107"),sQuery(id+"F6.wireOp",EDGE,"E7.sketch_text.stroke-108"),sQuery(id+"F6.wireOp",EDGE,"E7.sketch_text.stroke-109"),sQuery(id+"F6.wireOp",EDGE,"E7.sketch_text.stroke-110"),sQuery(id+"F6.wireOp",EDGE,"E7.sketch_text.stroke-111")])]});
            var Q5;
            Q5=makeQuery(id+"F10.opExtrude","SWEPT_BODY",BODY,{"disambiguationData":[OSD([sQuery(id+"F6.wireOp",EDGE,"E7.sketch_text.stroke-112"),sQuery(id+"F6.wireOp",EDGE,"E7.sketch_text.stroke-113"),sQuery(id+"F6.wireOp",EDGE,"E7.sketch_text.stroke-114"),sQuery(id+"F6.wireOp",EDGE,"E7.sketch_text.stroke-115"),sQuery(id+"F6.wireOp",EDGE,"E7.sketch_text.stroke-116"),sQuery(id+"F6.wireOp",EDGE,"E7.sketch_text.stroke-117"),sQuery(id+"F6.wireOp",EDGE,"E7.sketch_text.stroke-118"),sQuery(id+"F6.wireOp",EDGE,"E7.sketch_text.stroke-119"),sQuery(id+"F6.wireOp",EDGE,"E7.sketch_text.stroke-120"),sQuery(id+"F6.wireOp",EDGE,"E7.sketch_text.stroke-121"),sQuery(id+"F6.wireOp",EDGE,"E7.sketch_text.stroke-122"),sQuery(id+"F6.wireOp",EDGE,"E7.sketch_text.stroke-123"),sQuery(id+"F6.wireOp",EDGE,"E7.sketch_text.stroke-124"),sQuery(id+"F6.wireOp",EDGE,"E7.sketch_text.stroke-125"),sQuery(id+"F6.wireOp",EDGE,"E7.sketch_text.stroke-126"),sQuery(id+"F6.wireOp",EDGE,"E7.sketch_text.stroke-127"),sQuery(id+"F6.wireOp",EDGE,"E7.sketch_text.stroke-128"),sQuery(id+"F6.wireOp",EDGE,"E7.sketch_text.stroke-129"),sQuery(id+"F6.wireOp",EDGE,"E7.sketch_text.stroke-130"),sQuery(id+"F6.wireOp",EDGE,"E7.sketch_text.stroke-131"),sQuery(id+"F6.wireOp",EDGE,"E7.sketch_text.stroke-132"),sQuery(id+"F6.wireOp",EDGE,"E7.sketch_text.stroke-133"),sQuery(id+"F6.wireOp",EDGE,"E7.sketch_text.stroke-134"),sQuery(id+"F6.wireOp",EDGE,"E7.sketch_text.stroke-135"),sQuery(id+"F6.wireOp",EDGE,"E7.sketch_text.stroke-136"),sQuery(id+"F6.wireOp",EDGE,"E7.sketch_text.stroke-137")])]});
            var Q6;
            Q6=makeQuery(id+"F10.opExtrude","SWEPT_BODY",BODY,{"disambiguationData":[OSD([sQuery(id+"F6.wireOp",EDGE,"E7.sketch_text.stroke-138"),sQuery(id+"F6.wireOp",EDGE,"E7.sketch_text.stroke-139"),sQuery(id+"F6.wireOp",EDGE,"E7.sketch_text.stroke-140"),sQuery(id+"F6.wireOp",EDGE,"E7.sketch_text.stroke-141"),sQuery(id+"F6.wireOp",EDGE,"E7.sketch_text.stroke-142"),sQuery(id+"F6.wireOp",EDGE,"E7.sketch_text.stroke-143"),sQuery(id+"F6.wireOp",EDGE,"E7.sketch_text.stroke-144"),sQuery(id+"F6.wireOp",EDGE,"E7.sketch_text.stroke-145"),sQuery(id+"F6.wireOp",EDGE,"E7.sketch_text.stroke-146"),sQuery(id+"F6.wireOp",EDGE,"E7.sketch_text.stroke-147"),sQuery(id+"F6.wireOp",EDGE,"E7.sketch_text.stroke-148"),sQuery(id+"F6.wireOp",EDGE,"E7.sketch_text.stroke-149"),sQuery(id+"F6.wireOp",EDGE,"E7.sketch_text.stroke-150"),sQuery(id+"F6.wireOp",EDGE,"E7.sketch_text.stroke-151"),sQuery(id+"F6.wireOp",EDGE,"E7.sketch_text.stroke-152"),sQuery(id+"F6.wireOp",EDGE,"E7.sketch_text.stroke-153"),sQuery(id+"F6.wireOp",EDGE,"E7.sketch_text.stroke-154"),sQuery(id+"F6.wireOp",EDGE,"E7.sketch_text.stroke-155"),sQuery(id+"F6.wireOp",EDGE,"E7.sketch_text.stroke-156"),sQuery(id+"F6.wireOp",EDGE,"E7.sketch_text.stroke-157"),sQuery(id+"F6.wireOp",EDGE,"E7.sketch_text.stroke-158"),sQuery(id+"F6.wireOp",EDGE,"E7.sketch_text.stroke-159"),sQuery(id+"F6.wireOp",EDGE,"E7.sketch_text.stroke-160"),sQuery(id+"F6.wireOp",EDGE,"E7.sketch_text.stroke-161"),sQuery(id+"F6.wireOp",EDGE,"E7.sketch_text.stroke-162"),sQuery(id+"F6.wireOp",EDGE,"E7.sketch_text.stroke-163"),sQuery(id+"F6.wireOp",EDGE,"E7.sketch_text.stroke-164")])]});
            var Q7;
            Q7=makeQuery(id+"F10.opExtrude","SWEPT_BODY",BODY,{"disambiguationData":[OSD([sQuery(id+"F6.wireOp",EDGE,"E7.sketch_text.stroke-165"),sQuery(id+"F6.wireOp",EDGE,"E7.sketch_text.stroke-166"),sQuery(id+"F6.wireOp",EDGE,"E7.sketch_text.stroke-167"),sQuery(id+"F6.wireOp",EDGE,"E7.sketch_text.stroke-168"),sQuery(id+"F6.wireOp",EDGE,"E7.sketch_text.stroke-169"),sQuery(id+"F6.wireOp",EDGE,"E7.sketch_text.stroke-170"),sQuery(id+"F6.wireOp",EDGE,"E7.sketch_text.stroke-171"),sQuery(id+"F6.wireOp",EDGE,"E7.sketch_text.stroke-172"),sQuery(id+"F6.wireOp",EDGE,"E7.sketch_text.stroke-173"),sQuery(id+"F6.wireOp",EDGE,"E7.sketch_text.stroke-174"),sQuery(id+"F6.wireOp",EDGE,"E7.sketch_text.stroke-175"),sQuery(id+"F6.wireOp",EDGE,"E7.sketch_text.stroke-176"),sQuery(id+"F6.wireOp",EDGE,"E7.sketch_text.stroke-177"),sQuery(id+"F6.wireOp",EDGE,"E7.sketch_text.stroke-178"),sQuery(id+"F6.wireOp",EDGE,"E7.sketch_text.stroke-179"),sQuery(id+"F6.wireOp",EDGE,"E7.sketch_text.stroke-180"),sQuery(id+"F6.wireOp",EDGE,"E7.sketch_text.stroke-181"),sQuery(id+"F6.wireOp",EDGE,"E7.sketch_text.stroke-182"),sQuery(id+"F6.wireOp",EDGE,"E7.sketch_text.stroke-183"),sQuery(id+"F6.wireOp",EDGE,"E7.sketch_text.stroke-184")])]});
            var Q8;
            Q8=makeQuery(id+"F10.opExtrude","SWEPT_BODY",BODY,{"disambiguationData":[OSD([sQuery(id+"F7.wireOp",EDGE,"E9.sketch_text.stroke-0"),sQuery(id+"F7.wireOp",EDGE,"E9.sketch_text.stroke-1"),sQuery(id+"F7.wireOp",EDGE,"E9.sketch_text.stroke-2"),sQuery(id+"F7.wireOp",EDGE,"E9.sketch_text.stroke-3"),sQuery(id+"F7.wireOp",EDGE,"E9.sketch_text.stroke-4"),sQuery(id+"F7.wireOp",EDGE,"E9.sketch_text.stroke-5"),sQuery(id+"F7.wireOp",EDGE,"E9.sketch_text.stroke-6"),sQuery(id+"F7.wireOp",EDGE,"E9.sketch_text.stroke-7"),sQuery(id+"F7.wireOp",EDGE,"E9.sketch_text.stroke-8"),sQuery(id+"F7.wireOp",EDGE,"E9.sketch_text.stroke-9"),sQuery(id+"F7.wireOp",EDGE,"E9.sketch_text.stroke-10"),sQuery(id+"F7.wireOp",EDGE,"E9.sketch_text.stroke-11"),sQuery(id+"F7.wireOp",EDGE,"E9.sketch_text.stroke-12"),sQuery(id+"F7.wireOp",EDGE,"E9.sketch_text.stroke-13"),sQuery(id+"F7.wireOp",EDGE,"E9.sketch_text.stroke-14"),sQuery(id+"F7.wireOp",EDGE,"E9.sketch_text.stroke-15"),sQuery(id+"F7.wireOp",EDGE,"E9.sketch_text.stroke-16"),sQuery(id+"F7.wireOp",EDGE,"E9.sketch_text.stroke-17"),sQuery(id+"F7.wireOp",EDGE,"E9.sketch_text.stroke-18"),sQuery(id+"F7.wireOp",EDGE,"E9.sketch_text.stroke-19"),sQuery(id+"F7.wireOp",EDGE,"E9.sketch_text.stroke-20"),sQuery(id+"F7.wireOp",EDGE,"E9.sketch_text.stroke-21"),sQuery(id+"F7.wireOp",EDGE,"E9.sketch_text.stroke-22"),sQuery(id+"F7.wireOp",EDGE,"E9.sketch_text.stroke-23"),sQuery(id+"F7.wireOp",EDGE,"E9.sketch_text.stroke-24"),sQuery(id+"F7.wireOp",EDGE,"E9.sketch_text.stroke-25"),sQuery(id+"F7.wireOp",EDGE,"E9.sketch_text.stroke-26"),sQuery(id+"F7.wireOp",EDGE,"E9.sketch_text.stroke-27"),sQuery(id+"F7.wireOp",EDGE,"E9.sketch_text.stroke-28"),sQuery(id+"F7.wireOp",EDGE,"E9.sketch_text.stroke-29")])]});
            var Q9;
            Q9=makeQuery(id+"F10.opExtrude","SWEPT_BODY",BODY,{"disambiguationData":[OSD([sQuery(id+"F7.wireOp",EDGE,"E9.sketch_text.stroke-30"),sQuery(id+"F7.wireOp",EDGE,"E9.sketch_text.stroke-31"),sQuery(id+"F7.wireOp",EDGE,"E9.sketch_text.stroke-32"),sQuery(id+"F7.wireOp",EDGE,"E9.sketch_text.stroke-33"),sQuery(id+"F7.wireOp",EDGE,"E9.sketch_text.stroke-34"),sQuery(id+"F7.wireOp",EDGE,"E9.sketch_text.stroke-35"),sQuery(id+"F7.wireOp",EDGE,"E9.sketch_text.stroke-36"),sQuery(id+"F7.wireOp",EDGE,"E9.sketch_text.stroke-37"),sQuery(id+"F7.wireOp",EDGE,"E9.sketch_text.stroke-38"),sQuery(id+"F7.wireOp",EDGE,"E9.sketch_text.stroke-39"),sQuery(id+"F7.wireOp",EDGE,"E9.sketch_text.stroke-40"),sQuery(id+"F7.wireOp",EDGE,"E9.sketch_text.stroke-41"),sQuery(id+"F7.wireOp",EDGE,"E9.sketch_text.stroke-42"),sQuery(id+"F7.wireOp",EDGE,"E9.sketch_text.stroke-43"),sQuery(id+"F7.wireOp",EDGE,"E9.sketch_text.stroke-44"),sQuery(id+"F7.wireOp",EDGE,"E9.sketch_text.stroke-45"),sQuery(id+"F7.wireOp",EDGE,"E9.sketch_text.stroke-46"),sQuery(id+"F7.wireOp",EDGE,"E9.sketch_text.stroke-47"),sQuery(id+"F7.wireOp",EDGE,"E9.sketch_text.stroke-48"),sQuery(id+"F7.wireOp",EDGE,"E9.sketch_text.stroke-49")])]});
            var Q10;
            Q10=makeQuery(id+"F10.opExtrude","SWEPT_BODY",BODY,{"disambiguationData":[OSD([sQuery(id+"F7.wireOp",EDGE,"E9.sketch_text.stroke-50"),sQuery(id+"F7.wireOp",EDGE,"E9.sketch_text.stroke-51"),sQuery(id+"F7.wireOp",EDGE,"E9.sketch_text.stroke-52"),sQuery(id+"F7.wireOp",EDGE,"E9.sketch_text.stroke-53"),sQuery(id+"F7.wireOp",EDGE,"E9.sketch_text.stroke-54"),sQuery(id+"F7.wireOp",EDGE,"E9.sketch_text.stroke-55"),sQuery(id+"F7.wireOp",EDGE,"E9.sketch_text.stroke-56"),sQuery(id+"F7.wireOp",EDGE,"E9.sketch_text.stroke-57"),sQuery(id+"F7.wireOp",EDGE,"E9.sketch_text.stroke-58"),sQuery(id+"F7.wireOp",EDGE,"E9.sketch_text.stroke-59"),sQuery(id+"F7.wireOp",EDGE,"E9.sketch_text.stroke-60"),sQuery(id+"F7.wireOp",EDGE,"E9.sketch_text.stroke-61"),sQuery(id+"F7.wireOp",EDGE,"E9.sketch_text.stroke-62"),sQuery(id+"F7.wireOp",EDGE,"E9.sketch_text.stroke-63"),sQuery(id+"F7.wireOp",EDGE,"E9.sketch_text.stroke-64"),sQuery(id+"F7.wireOp",EDGE,"E9.sketch_text.stroke-65"),sQuery(id+"F7.wireOp",EDGE,"E9.sketch_text.stroke-66"),sQuery(id+"F7.wireOp",EDGE,"E9.sketch_text.stroke-67"),sQuery(id+"F7.wireOp",EDGE,"E9.sketch_text.stroke-68"),sQuery(id+"F7.wireOp",EDGE,"E9.sketch_text.stroke-69"),sQuery(id+"F7.wireOp",EDGE,"E9.sketch_text.stroke-70"),sQuery(id+"F7.wireOp",EDGE,"E9.sketch_text.stroke-71"),sQuery(id+"F7.wireOp",EDGE,"E9.sketch_text.stroke-72"),sQuery(id+"F7.wireOp",EDGE,"E9.sketch_text.stroke-73"),sQuery(id+"F7.wireOp",EDGE,"E9.sketch_text.stroke-74"),sQuery(id+"F7.wireOp",EDGE,"E9.sketch_text.stroke-75"),sQuery(id+"F7.wireOp",EDGE,"E9.sketch_text.stroke-76"),sQuery(id+"F7.wireOp",EDGE,"E9.sketch_text.stroke-77"),sQuery(id+"F7.wireOp",EDGE,"E9.sketch_text.stroke-78"),sQuery(id+"F7.wireOp",EDGE,"E9.sketch_text.stroke-79"),sQuery(id+"F7.wireOp",EDGE,"E9.sketch_text.stroke-80"),sQuery(id+"F7.wireOp",EDGE,"E9.sketch_text.stroke-81"),sQuery(id+"F7.wireOp",EDGE,"E9.sketch_text.stroke-82"),sQuery(id+"F7.wireOp",EDGE,"E9.sketch_text.stroke-83"),sQuery(id+"F7.wireOp",EDGE,"E9.sketch_text.stroke-84")])]});
            var Q11;
            Q11=makeQuery(id+"F10.opExtrude","SWEPT_BODY",BODY,{"disambiguationData":[OSD([sQuery(id+"F7.wireOp",EDGE,"E9.sketch_text.stroke-85"),sQuery(id+"F7.wireOp",EDGE,"E9.sketch_text.stroke-86"),sQuery(id+"F7.wireOp",EDGE,"E9.sketch_text.stroke-87"),sQuery(id+"F7.wireOp",EDGE,"E9.sketch_text.stroke-88"),sQuery(id+"F7.wireOp",EDGE,"E9.sketch_text.stroke-89"),sQuery(id+"F7.wireOp",EDGE,"E9.sketch_text.stroke-90"),sQuery(id+"F7.wireOp",EDGE,"E9.sketch_text.stroke-91"),sQuery(id+"F7.wireOp",EDGE,"E9.sketch_text.stroke-92"),sQuery(id+"F7.wireOp",EDGE,"E9.sketch_text.stroke-93"),sQuery(id+"F7.wireOp",EDGE,"E9.sketch_text.stroke-94"),sQuery(id+"F7.wireOp",EDGE,"E9.sketch_text.stroke-95"),sQuery(id+"F7.wireOp",EDGE,"E9.sketch_text.stroke-96"),sQuery(id+"F7.wireOp",EDGE,"E9.sketch_text.stroke-97"),sQuery(id+"F7.wireOp",EDGE,"E9.sketch_text.stroke-98"),sQuery(id+"F7.wireOp",EDGE,"E9.sketch_text.stroke-99"),sQuery(id+"F7.wireOp",EDGE,"E9.sketch_text.stroke-100"),sQuery(id+"F7.wireOp",EDGE,"E9.sketch_text.stroke-101"),sQuery(id+"F7.wireOp",EDGE,"E9.sketch_text.stroke-102"),sQuery(id+"F7.wireOp",EDGE,"E9.sketch_text.stroke-103")])]});
            var Q12;
            Q12=makeQuery(id+"F10.opExtrude","SWEPT_BODY",BODY,{"disambiguationData":[OSD([sQuery(id+"F7.wireOp",EDGE,"E9.sketch_text.stroke-104"),sQuery(id+"F7.wireOp",EDGE,"E9.sketch_text.stroke-105"),sQuery(id+"F7.wireOp",EDGE,"E9.sketch_text.stroke-106"),sQuery(id+"F7.wireOp",EDGE,"E9.sketch_text.stroke-107"),sQuery(id+"F7.wireOp",EDGE,"E9.sketch_text.stroke-108"),sQuery(id+"F7.wireOp",EDGE,"E9.sketch_text.stroke-109"),sQuery(id+"F7.wireOp",EDGE,"E9.sketch_text.stroke-110"),sQuery(id+"F7.wireOp",EDGE,"E9.sketch_text.stroke-111"),sQuery(id+"F7.wireOp",EDGE,"E9.sketch_text.stroke-112"),sQuery(id+"F7.wireOp",EDGE,"E9.sketch_text.stroke-113"),sQuery(id+"F7.wireOp",EDGE,"E9.sketch_text.stroke-114"),sQuery(id+"F7.wireOp",EDGE,"E9.sketch_text.stroke-115"),sQuery(id+"F7.wireOp",EDGE,"E9.sketch_text.stroke-116"),sQuery(id+"F7.wireOp",EDGE,"E9.sketch_text.stroke-117"),sQuery(id+"F7.wireOp",EDGE,"E9.sketch_text.stroke-118"),sQuery(id+"F7.wireOp",EDGE,"E9.sketch_text.stroke-119"),sQuery(id+"F7.wireOp",EDGE,"E9.sketch_text.stroke-120"),sQuery(id+"F7.wireOp",EDGE,"E9.sketch_text.stroke-121"),sQuery(id+"F7.wireOp",EDGE,"E9.sketch_text.stroke-122"),sQuery(id+"F7.wireOp",EDGE,"E9.sketch_text.stroke-123"),sQuery(id+"F7.wireOp",EDGE,"E9.sketch_text.stroke-124"),sQuery(id+"F7.wireOp",EDGE,"E9.sketch_text.stroke-125"),sQuery(id+"F7.wireOp",EDGE,"E9.sketch_text.stroke-126"),sQuery(id+"F7.wireOp",EDGE,"E9.sketch_text.stroke-127"),sQuery(id+"F7.wireOp",EDGE,"E9.sketch_text.stroke-128"),sQuery(id+"F7.wireOp",EDGE,"E9.sketch_text.stroke-129"),sQuery(id+"F7.wireOp",EDGE,"E9.sketch_text.stroke-130"),sQuery(id+"F7.wireOp",EDGE,"E9.sketch_text.stroke-131"),sQuery(id+"F7.wireOp",EDGE,"E9.sketch_text.stroke-132"),sQuery(id+"F7.wireOp",EDGE,"E9.sketch_text.stroke-133")])]});
            var Q13;
            Q13=makeQuery(id+"F10.opExtrude","SWEPT_BODY",BODY,{"disambiguationData":[OSD([sQuery(id+"F8.wireOp",EDGE,"E10.sketch_text.stroke-0"),sQuery(id+"F8.wireOp",EDGE,"E10.sketch_text.stroke-1"),sQuery(id+"F8.wireOp",EDGE,"E10.sketch_text.stroke-2"),sQuery(id+"F8.wireOp",EDGE,"E10.sketch_text.stroke-3"),sQuery(id+"F8.wireOp",EDGE,"E10.sketch_text.stroke-4"),sQuery(id+"F8.wireOp",EDGE,"E10.sketch_text.stroke-5"),sQuery(id+"F8.wireOp",EDGE,"E10.sketch_text.stroke-6"),sQuery(id+"F8.wireOp",EDGE,"E10.sketch_text.stroke-7"),sQuery(id+"F8.wireOp",EDGE,"E10.sketch_text.stroke-8"),sQuery(id+"F8.wireOp",EDGE,"E10.sketch_text.stroke-9"),sQuery(id+"F8.wireOp",EDGE,"E10.sketch_text.stroke-10"),sQuery(id+"F8.wireOp",EDGE,"E10.sketch_text.stroke-11"),sQuery(id+"F8.wireOp",EDGE,"E10.sketch_text.stroke-12"),sQuery(id+"F8.wireOp",EDGE,"E10.sketch_text.stroke-13"),sQuery(id+"F8.wireOp",EDGE,"E10.sketch_text.stroke-14"),sQuery(id+"F8.wireOp",EDGE,"E10.sketch_text.stroke-15"),sQuery(id+"F8.wireOp",EDGE,"E10.sketch_text.stroke-16"),sQuery(id+"F8.wireOp",EDGE,"E10.sketch_text.stroke-17"),sQuery(id+"F8.wireOp",EDGE,"E10.sketch_text.stroke-18"),sQuery(id+"F8.wireOp",EDGE,"E10.sketch_text.stroke-19"),sQuery(id+"F8.wireOp",EDGE,"E10.sketch_text.stroke-20"),sQuery(id+"F8.wireOp",EDGE,"E10.sketch_text.stroke-21"),sQuery(id+"F8.wireOp",EDGE,"E10.sketch_text.stroke-22")])]});
            var Q14;
            Q14=makeQuery(id+"F10.opExtrude","SWEPT_BODY",BODY,{"disambiguationData":[OSD([sQuery(id+"F8.wireOp",EDGE,"E10.sketch_text.stroke-23"),sQuery(id+"F8.wireOp",EDGE,"E10.sketch_text.stroke-24"),sQuery(id+"F8.wireOp",EDGE,"E10.sketch_text.stroke-25"),sQuery(id+"F8.wireOp",EDGE,"E10.sketch_text.stroke-26"),sQuery(id+"F8.wireOp",EDGE,"E10.sketch_text.stroke-27"),sQuery(id+"F8.wireOp",EDGE,"E10.sketch_text.stroke-28"),sQuery(id+"F8.wireOp",EDGE,"E10.sketch_text.stroke-29"),sQuery(id+"F8.wireOp",EDGE,"E10.sketch_text.stroke-30"),sQuery(id+"F8.wireOp",EDGE,"E10.sketch_text.stroke-31"),sQuery(id+"F8.wireOp",EDGE,"E10.sketch_text.stroke-32"),sQuery(id+"F8.wireOp",EDGE,"E10.sketch_text.stroke-33"),sQuery(id+"F8.wireOp",EDGE,"E10.sketch_text.stroke-34"),sQuery(id+"F8.wireOp",EDGE,"E10.sketch_text.stroke-35"),sQuery(id+"F8.wireOp",EDGE,"E10.sketch_text.stroke-36"),sQuery(id+"F8.wireOp",EDGE,"E10.sketch_text.stroke-37"),sQuery(id+"F8.wireOp",EDGE,"E10.sketch_text.stroke-38"),sQuery(id+"F8.wireOp",EDGE,"E10.sketch_text.stroke-39"),sQuery(id+"F8.wireOp",EDGE,"E10.sketch_text.stroke-40"),sQuery(id+"F8.wireOp",EDGE,"E10.sketch_text.stroke-41"),sQuery(id+"F8.wireOp",EDGE,"E10.sketch_text.stroke-42")])]});
            var Q15;
            Q15=makeQuery(id+"F10.opExtrude","SWEPT_BODY",BODY,{"disambiguationData":[OSD([sQuery(id+"F8.wireOp",EDGE,"E10.sketch_text.stroke-43"),sQuery(id+"F8.wireOp",EDGE,"E10.sketch_text.stroke-44"),sQuery(id+"F8.wireOp",EDGE,"E10.sketch_text.stroke-45"),sQuery(id+"F8.wireOp",EDGE,"E10.sketch_text.stroke-46"),sQuery(id+"F8.wireOp",EDGE,"E10.sketch_text.stroke-47"),sQuery(id+"F8.wireOp",EDGE,"E10.sketch_text.stroke-48"),sQuery(id+"F8.wireOp",EDGE,"E10.sketch_text.stroke-49"),sQuery(id+"F8.wireOp",EDGE,"E10.sketch_text.stroke-50"),sQuery(id+"F8.wireOp",EDGE,"E10.sketch_text.stroke-51"),sQuery(id+"F8.wireOp",EDGE,"E10.sketch_text.stroke-52")])]});
            var Q16;
            Q16=makeQuery(id+"F10.opExtrude","SWEPT_BODY",BODY,{"disambiguationData":[OSD([sQuery(id+"F8.wireOp",EDGE,"E10.sketch_text.stroke-53"),sQuery(id+"F8.wireOp",EDGE,"E10.sketch_text.stroke-54"),sQuery(id+"F8.wireOp",EDGE,"E10.sketch_text.stroke-55"),sQuery(id+"F8.wireOp",EDGE,"E10.sketch_text.stroke-56"),sQuery(id+"F8.wireOp",EDGE,"E10.sketch_text.stroke-57"),sQuery(id+"F8.wireOp",EDGE,"E10.sketch_text.stroke-58"),sQuery(id+"F8.wireOp",EDGE,"E10.sketch_text.stroke-59"),sQuery(id+"F8.wireOp",EDGE,"E10.sketch_text.stroke-60"),sQuery(id+"F8.wireOp",EDGE,"E10.sketch_text.stroke-61"),sQuery(id+"F8.wireOp",EDGE,"E10.sketch_text.stroke-62"),sQuery(id+"F8.wireOp",EDGE,"E10.sketch_text.stroke-63"),sQuery(id+"F8.wireOp",EDGE,"E10.sketch_text.stroke-64"),sQuery(id+"F8.wireOp",EDGE,"E10.sketch_text.stroke-65"),sQuery(id+"F8.wireOp",EDGE,"E10.sketch_text.stroke-66"),sQuery(id+"F8.wireOp",EDGE,"E10.sketch_text.stroke-67"),sQuery(id+"F8.wireOp",EDGE,"E10.sketch_text.stroke-68"),sQuery(id+"F8.wireOp",EDGE,"E10.sketch_text.stroke-69"),sQuery(id+"F8.wireOp",EDGE,"E10.sketch_text.stroke-70"),sQuery(id+"F8.wireOp",EDGE,"E10.sketch_text.stroke-71"),sQuery(id+"F8.wireOp",EDGE,"E10.sketch_text.stroke-72"),sQuery(id+"F8.wireOp",EDGE,"E10.sketch_text.stroke-73"),sQuery(id+"F8.wireOp",EDGE,"E10.sketch_text.stroke-74"),sQuery(id+"F8.wireOp",EDGE,"E10.sketch_text.stroke-75"),sQuery(id+"F8.wireOp",EDGE,"E10.sketch_text.stroke-76"),sQuery(id+"F8.wireOp",EDGE,"E10.sketch_text.stroke-77"),sQuery(id+"F8.wireOp",EDGE,"E10.sketch_text.stroke-78")])]});
            var Q17;
            Q17=makeQuery(id+"F10.opExtrude","SWEPT_BODY",BODY,{"disambiguationData":[OSD([sQuery(id+"F8.wireOp",EDGE,"E10.sketch_text.stroke-79"),sQuery(id+"F8.wireOp",EDGE,"E10.sketch_text.stroke-80"),sQuery(id+"F8.wireOp",EDGE,"E10.sketch_text.stroke-81"),sQuery(id+"F8.wireOp",EDGE,"E10.sketch_text.stroke-82")])]});
            var Q18;
            Q18=makeQuery(id+"F10.opExtrude","SWEPT_BODY",BODY,{"disambiguationData":[OSD([sQuery(id+"F8.wireOp",EDGE,"E10.sketch_text.stroke-83"),sQuery(id+"F8.wireOp",EDGE,"E10.sketch_text.stroke-84"),sQuery(id+"F8.wireOp",EDGE,"E10.sketch_text.stroke-85"),sQuery(id+"F8.wireOp",EDGE,"E10.sketch_text.stroke-86"),sQuery(id+"F8.wireOp",EDGE,"E10.sketch_text.stroke-87"),sQuery(id+"F8.wireOp",EDGE,"E10.sketch_text.stroke-88"),sQuery(id+"F8.wireOp",EDGE,"E10.sketch_text.stroke-89"),sQuery(id+"F8.wireOp",EDGE,"E10.sketch_text.stroke-90"),sQuery(id+"F8.wireOp",EDGE,"E10.sketch_text.stroke-91"),sQuery(id+"F8.wireOp",EDGE,"E10.sketch_text.stroke-92"),sQuery(id+"F8.wireOp",EDGE,"E10.sketch_text.stroke-93"),sQuery(id+"F8.wireOp",EDGE,"E10.sketch_text.stroke-94"),sQuery(id+"F8.wireOp",EDGE,"E10.sketch_text.stroke-95"),sQuery(id+"F8.wireOp",EDGE,"E10.sketch_text.stroke-96"),sQuery(id+"F8.wireOp",EDGE,"E10.sketch_text.stroke-97"),sQuery(id+"F8.wireOp",EDGE,"E10.sketch_text.stroke-98"),sQuery(id+"F8.wireOp",EDGE,"E10.sketch_text.stroke-99"),sQuery(id+"F8.wireOp",EDGE,"E10.sketch_text.stroke-100"),sQuery(id+"F8.wireOp",EDGE,"E10.sketch_text.stroke-101"),sQuery(id+"F8.wireOp",EDGE,"E10.sketch_text.stroke-102"),sQuery(id+"F8.wireOp",EDGE,"E10.sketch_text.stroke-103"),sQuery(id+"F8.wireOp",EDGE,"E10.sketch_text.stroke-104"),sQuery(id+"F8.wireOp",EDGE,"E10.sketch_text.stroke-105")])]});
            var Q19;
            Q19=makeQuery(id+"F10.opExtrude","SWEPT_BODY",BODY,{"disambiguationData":[OSD([sQuery(id+"F8.wireOp",EDGE,"E10.sketch_text.stroke-106"),sQuery(id+"F8.wireOp",EDGE,"E10.sketch_text.stroke-107"),sQuery(id+"F8.wireOp",EDGE,"E10.sketch_text.stroke-108"),sQuery(id+"F8.wireOp",EDGE,"E10.sketch_text.stroke-109"),sQuery(id+"F8.wireOp",EDGE,"E10.sketch_text.stroke-110"),sQuery(id+"F8.wireOp",EDGE,"E10.sketch_text.stroke-111"),sQuery(id+"F8.wireOp",EDGE,"E10.sketch_text.stroke-112"),sQuery(id+"F8.wireOp",EDGE,"E10.sketch_text.stroke-113"),sQuery(id+"F8.wireOp",EDGE,"E10.sketch_text.stroke-114"),sQuery(id+"F8.wireOp",EDGE,"E10.sketch_text.stroke-115"),sQuery(id+"F8.wireOp",EDGE,"E10.sketch_text.stroke-116"),sQuery(id+"F8.wireOp",EDGE,"E10.sketch_text.stroke-117"),sQuery(id+"F8.wireOp",EDGE,"E10.sketch_text.stroke-118"),sQuery(id+"F8.wireOp",EDGE,"E10.sketch_text.stroke-119"),sQuery(id+"F8.wireOp",EDGE,"E10.sketch_text.stroke-120"),sQuery(id+"F8.wireOp",EDGE,"E10.sketch_text.stroke-121"),sQuery(id+"F8.wireOp",EDGE,"E10.sketch_text.stroke-122"),sQuery(id+"F8.wireOp",EDGE,"E10.sketch_text.stroke-123"),sQuery(id+"F8.wireOp",EDGE,"E10.sketch_text.stroke-124"),sQuery(id+"F8.wireOp",EDGE,"E10.sketch_text.stroke-125")])]});
            var Q20;
            Q20=makeQuery(id+"F10.opExtrude","SWEPT_BODY",BODY,{"disambiguationData":[OSD([sQuery(id+"F8.wireOp",EDGE,"E10.sketch_text.stroke-126"),sQuery(id+"F8.wireOp",EDGE,"E10.sketch_text.stroke-127"),sQuery(id+"F8.wireOp",EDGE,"E10.sketch_text.stroke-128"),sQuery(id+"F8.wireOp",EDGE,"E10.sketch_text.stroke-129"),sQuery(id+"F8.wireOp",EDGE,"E10.sketch_text.stroke-130"),sQuery(id+"F8.wireOp",EDGE,"E10.sketch_text.stroke-131"),sQuery(id+"F8.wireOp",EDGE,"E10.sketch_text.stroke-132"),sQuery(id+"F8.wireOp",EDGE,"E10.sketch_text.stroke-133"),sQuery(id+"F8.wireOp",EDGE,"E10.sketch_text.stroke-134"),sQuery(id+"F8.wireOp",EDGE,"E10.sketch_text.stroke-135")])]});
            var Q21;
            Q21=makeQuery(id+"F10.opExtrude","SWEPT_BODY",BODY,{"disambiguationData":[OSD([sQuery(id+"F8.wireOp",EDGE,"E10.sketch_text.stroke-136"),sQuery(id+"F8.wireOp",EDGE,"E10.sketch_text.stroke-137"),sQuery(id+"F8.wireOp",EDGE,"E10.sketch_text.stroke-138"),sQuery(id+"F8.wireOp",EDGE,"E10.sketch_text.stroke-139"),sQuery(id+"F8.wireOp",EDGE,"E10.sketch_text.stroke-140"),sQuery(id+"F8.wireOp",EDGE,"E10.sketch_text.stroke-141"),sQuery(id+"F8.wireOp",EDGE,"E10.sketch_text.stroke-142"),sQuery(id+"F8.wireOp",EDGE,"E10.sketch_text.stroke-143"),sQuery(id+"F8.wireOp",EDGE,"E10.sketch_text.stroke-144"),sQuery(id+"F8.wireOp",EDGE,"E10.sketch_text.stroke-145"),sQuery(id+"F8.wireOp",EDGE,"E10.sketch_text.stroke-146"),sQuery(id+"F8.wireOp",EDGE,"E10.sketch_text.stroke-147"),sQuery(id+"F8.wireOp",EDGE,"E10.sketch_text.stroke-148"),sQuery(id+"F8.wireOp",EDGE,"E10.sketch_text.stroke-149"),sQuery(id+"F8.wireOp",EDGE,"E10.sketch_text.stroke-150"),sQuery(id+"F8.wireOp",EDGE,"E10.sketch_text.stroke-151"),sQuery(id+"F8.wireOp",EDGE,"E10.sketch_text.stroke-152"),sQuery(id+"F8.wireOp",EDGE,"E10.sketch_text.stroke-153"),sQuery(id+"F8.wireOp",EDGE,"E10.sketch_text.stroke-154"),sQuery(id+"F8.wireOp",EDGE,"E10.sketch_text.stroke-155"),sQuery(id+"F8.wireOp",EDGE,"E10.sketch_text.stroke-156"),sQuery(id+"F8.wireOp",EDGE,"E10.sketch_text.stroke-157"),sQuery(id+"F8.wireOp",EDGE,"E10.sketch_text.stroke-158"),sQuery(id+"F8.wireOp",EDGE,"E10.sketch_text.stroke-159"),sQuery(id+"F8.wireOp",EDGE,"E10.sketch_text.stroke-160"),sQuery(id+"F8.wireOp",EDGE,"E10.sketch_text.stroke-161"),sQuery(id+"F8.wireOp",EDGE,"E10.sketch_text.stroke-162"),sQuery(id+"F8.wireOp",EDGE,"E10.sketch_text.stroke-163")])]});
            var Q22;
            Q22=makeQuery(id+"F5.opBoolean","INTERSECT",BODY,{"derivedFrom":[makeQuery(id+"F1.opExtrude","SWEPT_BODY",BODY,{"disambiguationData":[OSD([sQuery(id+"F0.wireOp",EDGE,"E0"),sQuery(id+"F0.wireOp",EDGE,"E1"),sQuery(id+"F0.wireOp",EDGE,"E2"),sQuery(id+"F0.wireOp",EDGE,"E3"),sQuery(id+"F0.wireOp",EDGE,"E4")])]}),makeQuery(id+"F4.opRevolve","SWEPT_BODY",BODY,{"disambiguationData":[OSD([sQuery(id+"F2.wireOp",EDGE,"E5"),sQuery(id+"F2.wireOp",EDGE,"E6")])]})]});
            booleanBodies(context, id + "F12", {"operationType" : BooleanOperationType.SUBTRACTION, "tools" : qUnion([Q0, Q1, Q2, Q3, Q4, Q5, Q6, Q7, Q8, Q9, Q10, Q11, Q12, Q13, Q14, Q15, Q16, Q17, Q18, Q19, Q20, Q21]), "targets" : qUnion([Q22])});
        }
        {
            var Q0;
            Q0=qCreatedBy(makeId("Top.planeOp"),FACE);
            var sketch = newSketch(context, id + "F13", { "sketchPlane" : qUnion([Q0])});
            skCircle(sketch, "E11", {"center": v(0, 0) * mm, "radius": 19.69 * mm});
            skSolve(sketch);
        }
        {
            var Q0;
            Q0=makeQuery(id+"F13.imprint","IMPRINT",FACE,{"disambiguationData":[TD([[makeQuery(id+"F13.imprint","IMPRINT",EDGE,{"derivedFrom":sQuery(id+"F13.wireOp",EDGE,"E11")}),1.0]])]});
            var Q1;
            Q1=sQuery(id+"F13.wireOp",EDGE,"E11");
            extrude(context, id + "F14", {"entities" : qUnion([Q0]), "surfaceEntities" : qUnion([Q1]), "depth" : 6.35 * mm});
        }
        {
            var Q0;
            Q0=makeQuery(id+"F14.opExtrude","SWEPT_BODY",BODY,{"disambiguationData":[OSD([sQuery(id+"F13.wireOp",EDGE,"E11")])]});
            var Q1;
            Q1=makeQuery(id+"F1.opExtrude","CAP_FACE",FACE,{"disambiguationData":[OSD([sQuery(id+"F0.wireOp",EDGE,"E0"),sQuery(id+"F0.wireOp",EDGE,"E1"),sQuery(id+"F0.wireOp",EDGE,"E2"),sQuery(id+"F0.wireOp",EDGE,"E3"),sQuery(id+"F0.wireOp",EDGE,"E4")])],"isStart":true});
            transform(context, id + "F15", {"entities" : qUnion([Q0]), "transformType" : TransformType.TRANSLATION_DISTANCE, "transformDirection" : qUnion([Q1]), "distance" : 52.24 * mm, "makeCopy" : false});
        }
        {
            var Q0;
            Q0=makeQuery(id+"F14.opExtrude","SWEPT_BODY",BODY,{"disambiguationData":[OSD([sQuery(id+"F13.wireOp",EDGE,"E11")])]});
            var Q1;
            Q1=makeQuery(id+"F5.opBoolean","INTERSECT",BODY,{"derivedFrom":[makeQuery(id+"F1.opExtrude","SWEPT_BODY",BODY,{"disambiguationData":[OSD([sQuery(id+"F0.wireOp",EDGE,"E0"),sQuery(id+"F0.wireOp",EDGE,"E1"),sQuery(id+"F0.wireOp",EDGE,"E2"),sQuery(id+"F0.wireOp",EDGE,"E3"),sQuery(id+"F0.wireOp",EDGE,"E4")])]}),makeQuery(id+"F4.opRevolve","SWEPT_BODY",BODY,{"disambiguationData":[OSD([sQuery(id+"F2.wireOp",EDGE,"E5"),sQuery(id+"F2.wireOp",EDGE,"E6")])]})]});
            booleanBodies(context, id + "F16", {"operationType" : BooleanOperationType.SUBTRACTION, "tools" : qUnion([Q0]), "targets" : qUnion([Q1])});
        }
        {
            var Q0;
            Q0=qCreatedBy(makeId("Top.planeOp"),FACE);
            var sketch = newSketch(context, id + "F17", { "sketchPlane" : qUnion([Q0])});
            skPoint(sketch, "E12", {"position": v(0, 29.5) * mm});
            skCircle(sketch, "E13", {"center": v(0, 29.5) * mm, "radius": 3.63 * mm});
            skCircle(sketch, "E14", {"center": v(0, 34.74) * mm, "radius": 1.48 * mm});
            skLineSegment(sketch, "E15", {"start": v(-1.48, 34.74) * mm, "end": v(-3.26, 31.1) * mm});
            skLineSegment(sketch, "E16", {"start": v(1.48, 34.74) * mm, "end": v(3.26, 31.1) * mm});
            skSolve(sketch);
        }
        {
            var Q0;
            {var subQ0=sQuery(id+"F17.wireOp",EDGE,"E14");var subQ1=makeQuery(id+"F17.imprint","INTERSECT",VERTEX,{"derivedFrom":[subQ0,sQuery(id+"F17.wireOp",EDGE,"E15")]});Q0=makeQuery(id+"F17.imprint","IMPRINT",FACE,{"disambiguationData":[TD([[makeQuery(id+"F17.imprint","IMPRINT",EDGE,{"disambiguationData":[TD([[subQ1,1.0]])],"derivedFrom":subQ0}),1.0]])]});}
            var Q1;
            {var subQ0=sQuery(id+"F17.wireOp",EDGE,"E15");Q1=makeQuery(id+"F17.imprint","IMPRINT",FACE,{"disambiguationData":[TD([[makeQuery(id+"F17.imprint","IMPRINT",EDGE,{"derivedFrom":subQ0}),1.0]])]});}
            var Q2;
            {var subQ0=sQuery(id+"F17.wireOp",EDGE,"E13");var subQ1=makeQuery(id+"F17.imprint","INTERSECT",VERTEX,{"derivedFrom":[subQ0,sQuery(id+"F17.wireOp",EDGE,"E15")]});Q2=makeQuery(id+"F17.imprint","IMPRINT",FACE,{"disambiguationData":[TD([[makeQuery(id+"F17.imprint","IMPRINT",EDGE,{"disambiguationData":[TD([[subQ1,1.0]])],"derivedFrom":subQ0}),1.0]])]});}
            extrude(context, id + "F18", {"entities" : qUnion([Q0, Q1, Q2]), "depth" : 3.8 * mm});
        }
        {
            var Q0;
            Q0=makeQuery(id+"F18.opExtrude","SWEPT_BODY",BODY,{"disambiguationData":[OSD([sQuery(id+"F17.wireOp",EDGE,"E13"),sQuery(id+"F17.wireOp",EDGE,"E14"),sQuery(id+"F17.wireOp",EDGE,"E15"),sQuery(id+"F17.wireOp",EDGE,"E16")])]});
            var Q1;
            Q1=makeQuery(id+"F1.opExtrude","CAP_FACE",FACE,{"disambiguationData":[OSD([sQuery(id+"F0.wireOp",EDGE,"E0"),sQuery(id+"F0.wireOp",EDGE,"E1"),sQuery(id+"F0.wireOp",EDGE,"E2"),sQuery(id+"F0.wireOp",EDGE,"E3"),sQuery(id+"F0.wireOp",EDGE,"E4")])],"isStart":true});
            transform(context, id + "F19", {"entities" : qUnion([Q0]), "transformType" : TransformType.TRANSLATION_DISTANCE, "transformDirection" : qUnion([Q1]), "distance" : 51.48 * mm, "makeCopy" : false});
        }
        {
            var Q0;
            Q0=makeQuery(id+"F18.opExtrude","SWEPT_BODY",BODY,{"disambiguationData":[OSD([sQuery(id+"F17.wireOp",EDGE,"E13"),sQuery(id+"F17.wireOp",EDGE,"E14"),sQuery(id+"F17.wireOp",EDGE,"E15"),sQuery(id+"F17.wireOp",EDGE,"E16")])]});
            var Q1;
            Q1=makeQuery(id+"F5.opBoolean","INTERSECT",BODY,{"derivedFrom":[makeQuery(id+"F1.opExtrude","SWEPT_BODY",BODY,{"disambiguationData":[OSD([sQuery(id+"F0.wireOp",EDGE,"E0"),sQuery(id+"F0.wireOp",EDGE,"E1"),sQuery(id+"F0.wireOp",EDGE,"E2"),sQuery(id+"F0.wireOp",EDGE,"E3"),sQuery(id+"F0.wireOp",EDGE,"E4")])]}),makeQuery(id+"F4.opRevolve","SWEPT_BODY",BODY,{"disambiguationData":[OSD([sQuery(id+"F2.wireOp",EDGE,"E5"),sQuery(id+"F2.wireOp",EDGE,"E6")])]})]});
            booleanBodies(context, id + "F20", {"operationType" : BooleanOperationType.SUBTRACTION, "tools" : qUnion([Q0]), "targets" : qUnion([Q1])});
        }
        {
            var Q0;
            Q0=qCreatedBy(makeId("Top.planeOp"),FACE);
            var sketch = newSketch(context, id + "F21", { "sketchPlane" : qUnion([Q0])});
            skCircle(sketch, "E17", {"center": v(0, 29.5) * mm, "radius": 3.62 * mm});
            skCircle(sketch, "E18", {"center": v(0, 34.71) * mm, "radius": 3.62 * mm});
            skLineSegment(sketch, "E19", {"start": v(-3.62, 29.4) * mm, "end": v(-3.62, 34.71) * mm});
            skLineSegment(sketch, "E20", {"start": v(3.62, 29.62) * mm, "end": v(3.62, 34.71) * mm});
            skSolve(sketch);
        }
        {
            var Q0;
            {var subQ1=sQuery(id+"F21.wireOp",EDGE,"E17");var subQ7=makeQuery(id+"F21.imprint","INTERSECT",VERTEX,{"derivedFrom":[subQ1,sQuery(id+"F21.wireOp",EDGE,"E20")]});Q0=makeQuery(id+"F21.imprint","IMPRINT",FACE,{"disambiguationData":[TD([[makeQuery(id+"F21.imprint","IMPRINT",EDGE,{"disambiguationData":[TD([[subQ7,-1.0]])],"derivedFrom":subQ1}),1.0]])]});}
            var Q1;
            {var subQ0=sQuery(id+"F21.wireOp",EDGE,"E18");var subQ1=sQuery(id+"F21.wireOp",EDGE,"E17");var subQ2=makeQuery(id+"F21.imprint","INTERSECT",VERTEX,{"disambiguationData":[OD(0.0)],"derivedFrom":[subQ1,subQ0]});Q1=makeQuery(id+"F21.imprint","IMPRINT",FACE,{"disambiguationData":[TD([[makeQuery(id+"F21.imprint","IMPRINT",EDGE,{"disambiguationData":[TD([[subQ2,-1.0]])],"derivedFrom":subQ1}),-1.0]])]});}
            var Q2;
            {var subQ0=sQuery(id+"F21.wireOp",EDGE,"E18");var subQ1=sQuery(id+"F21.wireOp",EDGE,"E17");var subQ2=makeQuery(id+"F21.imprint","INTERSECT",VERTEX,{"disambiguationData":[OD(0.0)],"derivedFrom":[subQ1,subQ0]});Q2=makeQuery(id+"F21.imprint","IMPRINT",FACE,{"disambiguationData":[TD([[makeQuery(id+"F21.imprint","IMPRINT",EDGE,{"disambiguationData":[TD([[subQ2,-1.0]])],"derivedFrom":subQ1}),1.0]])]});}
            var Q3;
            {var subQ0=sQuery(id+"F21.wireOp",EDGE,"E19");var subQ1=sQuery(id+"F21.wireOp",EDGE,"E17");var subQ2=makeQuery(id+"F21.imprint","INTERSECT",VERTEX,{"disambiguationData":[OD(1.0)],"derivedFrom":[subQ1,subQ0]});Q3=makeQuery(id+"F21.imprint","IMPRINT",FACE,{"disambiguationData":[TD([[makeQuery(id+"F21.imprint","IMPRINT",EDGE,{"disambiguationData":[TD([[subQ2,1.0]])],"derivedFrom":subQ1}),-1.0]])]});}
            var Q4;
            {var subQ0=sQuery(id+"F21.wireOp",EDGE,"E20");Q4=makeQuery(id+"F21.imprint","IMPRINT",FACE,{"disambiguationData":[TD([[makeQuery(id+"F21.imprint","IMPRINT",EDGE,{"derivedFrom":subQ0}),1.0]])]});}
            extrude(context, id + "F22", {"entities" : qUnion([Q0, Q1, Q2, Q3, Q4]), "depth" : 2.81 * mm});
        }
        {
            var Q0;
            Q0=makeQuery(id+"F22.opExtrude","SWEPT_BODY",BODY,{"disambiguationData":[OSD([sQuery(id+"F21.wireOp",EDGE,"E17"),sQuery(id+"F21.wireOp",EDGE,"E18"),sQuery(id+"F21.wireOp",EDGE,"E19"),sQuery(id+"F21.wireOp",EDGE,"E20")])]});
            var Q1;
            Q1=makeQuery(id+"F1.opExtrude","CAP_FACE",FACE,{"disambiguationData":[OSD([sQuery(id+"F0.wireOp",EDGE,"E0"),sQuery(id+"F0.wireOp",EDGE,"E1"),sQuery(id+"F0.wireOp",EDGE,"E2"),sQuery(id+"F0.wireOp",EDGE,"E3"),sQuery(id+"F0.wireOp",EDGE,"E4")])],"isStart":true});
            transform(context, id + "F23", {"entities" : qUnion([Q0]), "transformType" : TransformType.TRANSLATION_DISTANCE, "transformDirection" : qUnion([Q1]), "distance" : 49.63 * mm, "makeCopy" : false});
        }
        {
            var Q0;
            Q0=makeQuery(id+"F22.opExtrude","SWEPT_BODY",BODY,{"disambiguationData":[OSD([sQuery(id+"F21.wireOp",EDGE,"E17"),sQuery(id+"F21.wireOp",EDGE,"E18"),sQuery(id+"F21.wireOp",EDGE,"E19"),sQuery(id+"F21.wireOp",EDGE,"E20")])]});
            var Q1;
            Q1=makeQuery(id+"F5.opBoolean","INTERSECT",BODY,{"derivedFrom":[makeQuery(id+"F1.opExtrude","SWEPT_BODY",BODY,{"disambiguationData":[OSD([sQuery(id+"F0.wireOp",EDGE,"E0"),sQuery(id+"F0.wireOp",EDGE,"E1"),sQuery(id+"F0.wireOp",EDGE,"E2"),sQuery(id+"F0.wireOp",EDGE,"E3"),sQuery(id+"F0.wireOp",EDGE,"E4")])]}),makeQuery(id+"F4.opRevolve","SWEPT_BODY",BODY,{"disambiguationData":[OSD([sQuery(id+"F2.wireOp",EDGE,"E5"),sQuery(id+"F2.wireOp",EDGE,"E6")])]})]});
            booleanBodies(context, id + "F24", {"operationType" : BooleanOperationType.SUBTRACTION, "tools" : qUnion([Q0]), "targets" : qUnion([Q1])});
        }
    });
